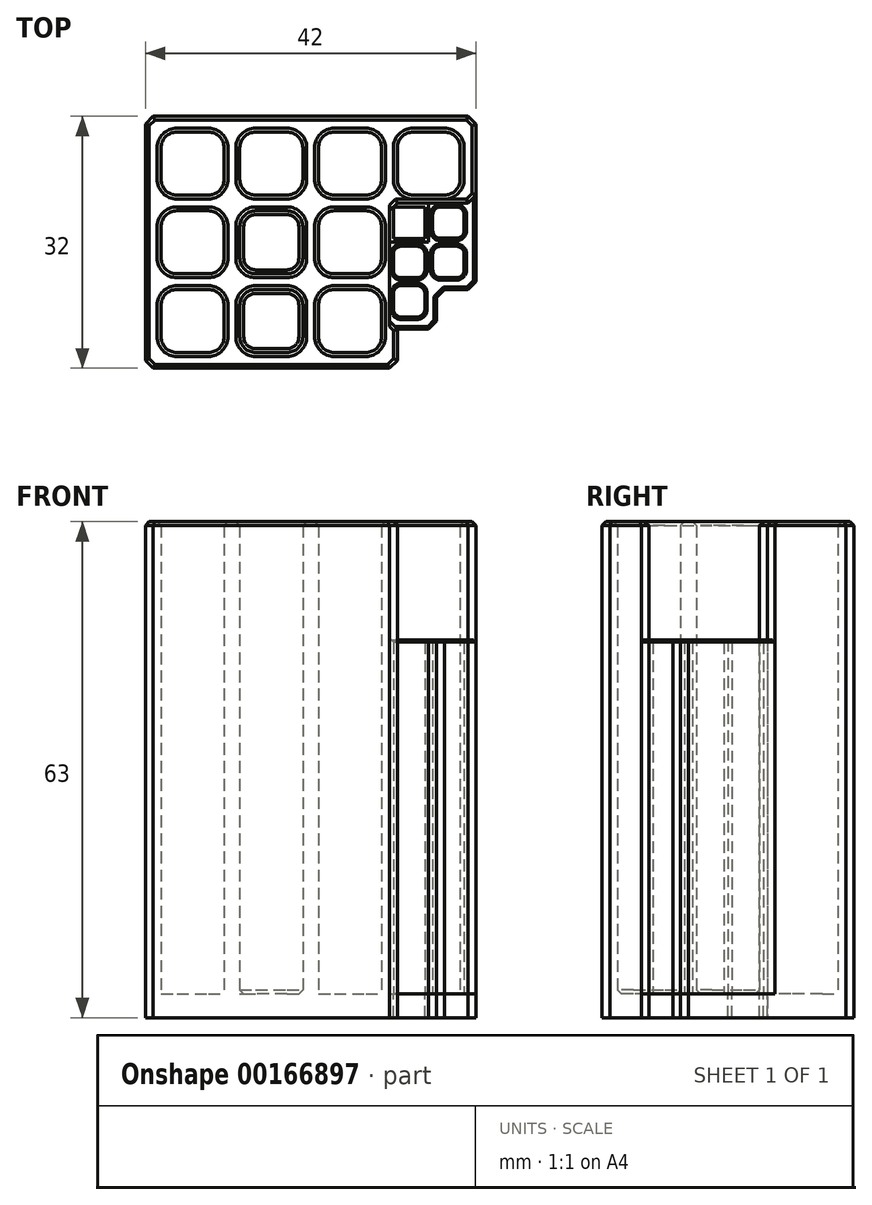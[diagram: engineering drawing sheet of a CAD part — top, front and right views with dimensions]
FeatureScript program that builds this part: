
annotation { "Feature Type Name" : "Feature", "Feature Type Description" : "" }
export const myFeature = defineFeature(function(context is Context, id is Id, definition is map)
    precondition{}
    {
        {
            var Q0;
            Q0=qCreatedBy(makeId("Top.planeOp"),FACE);
            var sketch = newSketch(context, id + "F0", { "sketchPlane" : qUnion([Q0])});
            skLineSegment(sketch, "E0.bottom", {"start": v(-42.55, 29) * mm, "end": v(-34.55, 29) * mm});
            skLineSegment(sketch, "E0.top", {"start": v(-42.55, 21) * mm, "end": v(-34.55, 21) * mm});
            skLineSegment(sketch, "E0.left", {"start": v(-42.55, 29) * mm, "end": v(-42.55, 21) * mm});
            skLineSegment(sketch, "E0.right", {"start": v(-34.55, 29) * mm, "end": v(-34.55, 21) * mm});
            skLineSegment(sketch, "E1", {"start": v(-42.55, 29) * mm, "end": v(-34.55, 21) * mm, "construction": true});
            skPoint(sketch, "E2", {"position": v(-38.55, 25) * mm});
            skLineSegment(sketch, "E3.bottom", {"start": v(-43.55, 30) * mm, "end": v(-33.55, 30) * mm});
            skLineSegment(sketch, "E3.top", {"start": v(-43.55, 20) * mm, "end": v(-33.55, 20) * mm});
            skLineSegment(sketch, "E3.left", {"start": v(-43.55, 30) * mm, "end": v(-43.55, 20) * mm});
            skLineSegment(sketch, "E3.right", {"start": v(-33.55, 30) * mm, "end": v(-33.55, 20) * mm});
            skLineSegment(sketch, "E4.bottom", {"start": v(-33.55, 30) * mm, "end": v(-23.55, 30) * mm});
            skLineSegment(sketch, "E4.top", {"start": v(-33.55, 20) * mm, "end": v(-23.55, 20) * mm});
            skLineSegment(sketch, "E4.right", {"start": v(-23.55, 30) * mm, "end": v(-23.55, 20) * mm});
            skLineSegment(sketch, "E5.bottom", {"start": v(-23.55, 30) * mm, "end": v(-13.55, 30) * mm});
            skLineSegment(sketch, "E5.top", {"start": v(-23.55, 20) * mm, "end": v(-13.55, 20) * mm});
            skLineSegment(sketch, "E5.right", {"start": v(-13.55, 30) * mm, "end": v(-13.55, 20) * mm});
            skLineSegment(sketch, "E6.top", {"start": v(-43.55, 10) * mm, "end": v(-33.55, 10) * mm});
            skLineSegment(sketch, "E6.left", {"start": v(-43.55, 20) * mm, "end": v(-43.55, 10) * mm});
            skLineSegment(sketch, "E6.right", {"start": v(-33.55, 20) * mm, "end": v(-33.55, 10) * mm});
            skLineSegment(sketch, "E7.top", {"start": v(-33.55, 10) * mm, "end": v(-23.55, 10) * mm});
            skLineSegment(sketch, "E7.right", {"start": v(-23.55, 20) * mm, "end": v(-23.55, 10) * mm});
            skLineSegment(sketch, "E8.top", {"start": v(-23.55, 10) * mm, "end": v(-13.55, 10) * mm});
            skLineSegment(sketch, "E8.right", {"start": v(-13.55, 20) * mm, "end": v(-13.55, 10) * mm});
            skLineSegment(sketch, "E9.top", {"start": v(-43.55, 0) * mm, "end": v(-33.55, 0) * mm});
            skLineSegment(sketch, "E9.left", {"start": v(-43.55, 10) * mm, "end": v(-43.55, 0) * mm});
            skLineSegment(sketch, "E9.right", {"start": v(-33.55, 10) * mm, "end": v(-33.55, 0) * mm});
            skLineSegment(sketch, "E10.top", {"start": v(-33.55, 0) * mm, "end": v(-23.55, 0) * mm});
            skLineSegment(sketch, "E10.right", {"start": v(-23.55, 10) * mm, "end": v(-23.55, 0) * mm});
            skLineSegment(sketch, "E11.top", {"start": v(-23.55, 0) * mm, "end": v(-13.55, 0) * mm});
            skLineSegment(sketch, "E11.right", {"start": v(-13.55, 10) * mm, "end": v(-13.55, 0) * mm});
            skLineSegment(sketch, "E12", {"start": v(-33.55, 30) * mm, "end": v(-23.55, 20) * mm, "construction": true});
            skLineSegment(sketch, "E13", {"start": v(-33.55, 20) * mm, "end": v(-23.55, 10) * mm, "construction": true});
            skLineSegment(sketch, "E14", {"start": v(-43.55, 20) * mm, "end": v(-33.55, 10) * mm, "construction": true});
            skLineSegment(sketch, "E15", {"start": v(-43.55, 10) * mm, "end": v(-33.55, 0) * mm, "construction": true});
            skLineSegment(sketch, "E16", {"start": v(-33.55, 10) * mm, "end": v(-23.55, 0) * mm, "construction": true});
            skLineSegment(sketch, "E17", {"start": v(-23.55, 10) * mm, "end": v(-13.55, 0) * mm, "construction": true});
            skLineSegment(sketch, "E18", {"start": v(-23.55, 20) * mm, "end": v(-13.55, 10) * mm, "construction": true});
            skPoint(sketch, "E19", {"position": v(-28.55, 25) * mm});
            skPoint(sketch, "E20", {"position": v(-18.55, 15) * mm});
            skPoint(sketch, "E21", {"position": v(-28.55, 15) * mm});
            skPoint(sketch, "E22", {"position": v(-38.55, 15) * mm});
            skPoint(sketch, "E23", {"position": v(-38.55, 5) * mm});
            skPoint(sketch, "E24", {"position": v(-28.55, 5) * mm});
            skPoint(sketch, "E25", {"position": v(-18.55, 5) * mm});
            skLineSegment(sketch, "E26.bottom", {"start": v(-24.55, 29) * mm, "end": v(-32.55, 29) * mm});
            skLineSegment(sketch, "E26.top", {"start": v(-24.55, 21) * mm, "end": v(-32.55, 21) * mm});
            skLineSegment(sketch, "E26.left", {"start": v(-24.55, 29) * mm, "end": v(-24.55, 21) * mm});
            skLineSegment(sketch, "E26.right", {"start": v(-32.55, 29) * mm, "end": v(-32.55, 21) * mm});
            skLineSegment(sketch, "E27", {"start": v(-23.55, 30) * mm, "end": v(-13.55, 20) * mm, "construction": true});
            skPoint(sketch, "E28", {"position": v(-18.55, 25) * mm});
            skLineSegment(sketch, "E29.bottom", {"start": v(-22.55, 29) * mm, "end": v(-14.55, 29) * mm});
            skLineSegment(sketch, "E29.top", {"start": v(-22.55, 21) * mm, "end": v(-14.55, 21) * mm});
            skLineSegment(sketch, "E29.left", {"start": v(-22.55, 29) * mm, "end": v(-22.55, 21) * mm});
            skLineSegment(sketch, "E29.right", {"start": v(-14.55, 29) * mm, "end": v(-14.55, 21) * mm});
            skLineSegment(sketch, "E30.bottom", {"start": v(-22.55, 19) * mm, "end": v(-14.55, 19) * mm});
            skLineSegment(sketch, "E30.top", {"start": v(-22.55, 11) * mm, "end": v(-14.55, 11) * mm});
            skLineSegment(sketch, "E30.left", {"start": v(-22.55, 19) * mm, "end": v(-22.55, 11) * mm});
            skLineSegment(sketch, "E30.right", {"start": v(-14.55, 19) * mm, "end": v(-14.55, 11) * mm});
            skLineSegment(sketch, "E31.bottom", {"start": v(-22.55, 9) * mm, "end": v(-14.55, 9) * mm});
            skLineSegment(sketch, "E31.top", {"start": v(-22.55, 1) * mm, "end": v(-14.55, 1) * mm});
            skLineSegment(sketch, "E31.left", {"start": v(-22.55, 9) * mm, "end": v(-22.55, 1) * mm});
            skLineSegment(sketch, "E31.right", {"start": v(-14.55, 9) * mm, "end": v(-14.55, 1) * mm});
            skLineSegment(sketch, "E32.bottom", {"start": v(-32.55, 9) * mm, "end": v(-24.55, 9) * mm});
            skLineSegment(sketch, "E32.top", {"start": v(-32.55, 1) * mm, "end": v(-24.55, 1) * mm});
            skLineSegment(sketch, "E32.left", {"start": v(-32.55, 9) * mm, "end": v(-32.55, 1) * mm});
            skLineSegment(sketch, "E32.right", {"start": v(-24.55, 9) * mm, "end": v(-24.55, 1) * mm});
            skLineSegment(sketch, "E33.bottom", {"start": v(-42.55, 9) * mm, "end": v(-34.55, 9) * mm});
            skLineSegment(sketch, "E33.top", {"start": v(-42.55, 1) * mm, "end": v(-34.55, 1) * mm});
            skLineSegment(sketch, "E33.left", {"start": v(-42.55, 9) * mm, "end": v(-42.55, 1) * mm});
            skLineSegment(sketch, "E33.right", {"start": v(-34.55, 9) * mm, "end": v(-34.55, 1) * mm});
            skLineSegment(sketch, "E34.bottom", {"start": v(-42.55, 19) * mm, "end": v(-34.55, 19) * mm});
            skLineSegment(sketch, "E34.top", {"start": v(-42.55, 11) * mm, "end": v(-34.55, 11) * mm});
            skLineSegment(sketch, "E34.left", {"start": v(-42.55, 19) * mm, "end": v(-42.55, 11) * mm});
            skLineSegment(sketch, "E34.right", {"start": v(-34.55, 19) * mm, "end": v(-34.55, 11) * mm});
            skLineSegment(sketch, "E35.bottom", {"start": v(-32.55, 19) * mm, "end": v(-24.55, 19) * mm});
            skLineSegment(sketch, "E35.top", {"start": v(-32.55, 11) * mm, "end": v(-24.55, 11) * mm});
            skLineSegment(sketch, "E35.left", {"start": v(-32.55, 19) * mm, "end": v(-32.55, 11) * mm});
            skLineSegment(sketch, "E35.right", {"start": v(-24.55, 19) * mm, "end": v(-24.55, 11) * mm});
            skLineSegment(sketch, "E36.left", {"start": v(-13.55, 0) * mm, "end": v(-13.55, 6) * mm});
            skLineSegment(sketch, "E37.left", {"start": v(-13.55, 6) * mm, "end": v(-13.55, 12) * mm});
            skLineSegment(sketch, "E38.left", {"start": v(-13.55, 12) * mm, "end": v(-13.55, 18) * mm});
            skLineSegment(sketch, "E39.bottom", {"start": v(-13.55, 30) * mm, "end": v(-3.55, 30) * mm});
            skLineSegment(sketch, "E39.top", {"start": v(-13.55, 20) * mm, "end": v(-3.55, 20) * mm});
            skLineSegment(sketch, "E39.right", {"start": v(-3.55, 30) * mm, "end": v(-3.55, 20) * mm});
            skLineSegment(sketch, "E40", {"start": v(-13.55, 30) * mm, "end": v(-3.55, 20) * mm, "construction": true});
            skPoint(sketch, "E41", {"position": v(-8.55, 25) * mm});
            skLineSegment(sketch, "E42.bottom", {"start": v(-4.55, 29) * mm, "end": v(-12.55, 29) * mm});
            skLineSegment(sketch, "E42.top", {"start": v(-4.55, 21) * mm, "end": v(-12.55, 21) * mm});
            skLineSegment(sketch, "E42.left", {"start": v(-4.55, 29) * mm, "end": v(-4.55, 21) * mm});
            skLineSegment(sketch, "E42.right", {"start": v(-12.55, 29) * mm, "end": v(-12.55, 21) * mm});
            skLineSegment(sketch, "E43.bottom", {"start": v(-13.55, 20) * mm, "end": v(-8.55, 20) * mm});
            skLineSegment(sketch, "E43.top", {"start": v(-13.55, 15) * mm, "end": v(-8.55, 15) * mm});
            skLineSegment(sketch, "E43.left", {"start": v(-13.55, 20) * mm, "end": v(-13.55, 15) * mm});
            skLineSegment(sketch, "E43.right", {"start": v(-8.55, 20) * mm, "end": v(-8.55, 15) * mm});
            skLineSegment(sketch, "E44.top", {"start": v(-13.55, 10) * mm, "end": v(-8.55, 10) * mm});
            skLineSegment(sketch, "E44.left", {"start": v(-13.55, 15) * mm, "end": v(-13.55, 10) * mm});
            skLineSegment(sketch, "E44.right", {"start": v(-8.55, 15) * mm, "end": v(-8.55, 10) * mm});
            skLineSegment(sketch, "E45.top", {"start": v(-13.55, 5) * mm, "end": v(-8.55, 5) * mm});
            skLineSegment(sketch, "E45.left", {"start": v(-13.55, 10) * mm, "end": v(-13.55, 5) * mm});
            skLineSegment(sketch, "E45.right", {"start": v(-8.55, 10) * mm, "end": v(-8.55, 5) * mm});
            skLineSegment(sketch, "E46.bottom", {"start": v(-8.55, 5) * mm, "end": v(-13.55, 5) * mm});
            skLineSegment(sketch, "E46.right", {"start": v(-13.55, 5) * mm, "end": v(-13.55, 0) * mm});
            skLineSegment(sketch, "E47.bottom", {"start": v(-8.55, 20) * mm, "end": v(-3.54, 20) * mm});
            skLineSegment(sketch, "E47.top", {"start": v(-8.55, 15) * mm, "end": v(-3.54, 15) * mm});
            skLineSegment(sketch, "E47.right", {"start": v(-3.54, 20) * mm, "end": v(-3.54, 15) * mm});
            skLineSegment(sketch, "E48.top", {"start": v(-8.55, 10) * mm, "end": v(-3.54, 10) * mm});
            skLineSegment(sketch, "E48.right", {"start": v(-3.54, 15) * mm, "end": v(-3.54, 10) * mm});
            skLineSegment(sketch, "E49", {"start": v(-13.55, 20) * mm, "end": v(-8.55, 15) * mm, "construction": true});
            skLineSegment(sketch, "E50", {"start": v(-13.55, 10) * mm, "end": v(-8.55, 5) * mm, "construction": true});
            skLineSegment(sketch, "E51", {"start": v(-8.55, 15) * mm, "end": v(-3.54, 10) * mm, "construction": true});
            skLineSegment(sketch, "E52", {"start": v(-13.55, 15) * mm, "end": v(-8.55, 10) * mm, "construction": true});
            skLineSegment(sketch, "E53", {"start": v(-8.55, 20) * mm, "end": v(-3.54, 15) * mm, "construction": true});
            skPoint(sketch, "E54", {"position": v(-11.05, 17.5) * mm});
            skPoint(sketch, "E55", {"position": v(-6.04, 17.5) * mm});
            skPoint(sketch, "E56", {"position": v(-11.05, 12.5) * mm});
            skPoint(sketch, "E57", {"position": v(-6.04, 12.5) * mm});
            skPoint(sketch, "E58", {"position": v(-11.05, 7.5) * mm});
            skLineSegment(sketch, "E59.bottom", {"start": v(-9.05, 19.5) * mm, "end": v(-13.05, 19.5) * mm});
            skLineSegment(sketch, "E59.top", {"start": v(-9.05, 15.5) * mm, "end": v(-13.05, 15.5) * mm});
            skLineSegment(sketch, "E59.left", {"start": v(-9.05, 19.5) * mm, "end": v(-9.05, 15.5) * mm});
            skLineSegment(sketch, "E59.right", {"start": v(-13.05, 19.5) * mm, "end": v(-13.05, 15.5) * mm});
            skLineSegment(sketch, "E60.bottom", {"start": v(-13.05, 14.5) * mm, "end": v(-9.05, 14.5) * mm});
            skLineSegment(sketch, "E60.top", {"start": v(-13.05, 10.5) * mm, "end": v(-9.05, 10.5) * mm});
            skLineSegment(sketch, "E60.left", {"start": v(-13.05, 14.5) * mm, "end": v(-13.05, 10.5) * mm});
            skLineSegment(sketch, "E60.right", {"start": v(-9.05, 14.5) * mm, "end": v(-9.05, 10.5) * mm});
            skLineSegment(sketch, "E61.bottom", {"start": v(-13.05, 9.5) * mm, "end": v(-9.05, 9.5) * mm});
            skLineSegment(sketch, "E61.top", {"start": v(-13.05, 5.5) * mm, "end": v(-9.05, 5.5) * mm});
            skLineSegment(sketch, "E61.left", {"start": v(-13.05, 9.5) * mm, "end": v(-13.05, 5.5) * mm});
            skLineSegment(sketch, "E61.right", {"start": v(-9.05, 9.5) * mm, "end": v(-9.05, 5.5) * mm});
            skLineSegment(sketch, "E62.bottom", {"start": v(-4.04, 15.5) * mm, "end": v(-8.04, 15.5) * mm});
            skLineSegment(sketch, "E62.top", {"start": v(-4.04, 19.5) * mm, "end": v(-8.04, 19.5) * mm});
            skLineSegment(sketch, "E62.left", {"start": v(-4.04, 15.5) * mm, "end": v(-4.04, 19.5) * mm});
            skLineSegment(sketch, "E62.right", {"start": v(-8.04, 15.5) * mm, "end": v(-8.04, 19.5) * mm});
            skLineSegment(sketch, "E63.bottom", {"start": v(-4.04, 10.5) * mm, "end": v(-8.04, 10.5) * mm});
            skLineSegment(sketch, "E63.top", {"start": v(-4.04, 14.5) * mm, "end": v(-8.04, 14.5) * mm});
            skLineSegment(sketch, "E63.left", {"start": v(-4.04, 10.5) * mm, "end": v(-4.04, 14.5) * mm});
            skLineSegment(sketch, "E63.right", {"start": v(-8.04, 10.5) * mm, "end": v(-8.04, 14.5) * mm});
            skLineSegment(sketch, "E64", {"start": v(-44.55, 30) * mm, "end": v(-44.55, 0) * mm});
            skLineSegment(sketch, "E65", {"start": v(-44.55, 0) * mm, "end": v(-44.55, -1) * mm});
            skLineSegment(sketch, "E66", {"start": v(-44.55, -1) * mm, "end": v(-13.55, -1) * mm});
            skLineSegment(sketch, "E67", {"start": v(-13.55, -1) * mm, "end": v(-12.55, -1) * mm});
            skLineSegment(sketch, "E68", {"start": v(-12.55, -1) * mm, "end": v(-12.55, 5) * mm});
            skLineSegment(sketch, "E69", {"start": v(-44.55, 30) * mm, "end": v(-44.55, 31) * mm});
            skLineSegment(sketch, "E70", {"start": v(-44.55, 31) * mm, "end": v(-3.55, 31) * mm});
            skLineSegment(sketch, "E71", {"start": v(-3.55, 31) * mm, "end": v(-2.55, 31) * mm});
            skLineSegment(sketch, "E72", {"start": v(-2.55, 31) * mm, "end": v(-2.55, 10) * mm});
            skLineSegment(sketch, "E73", {"start": v(-2.55, 10) * mm, "end": v(-2.55, 9) * mm});
            skLineSegment(sketch, "E74", {"start": v(-2.55, 9) * mm, "end": v(-8.55, 9) * mm});
            skLineSegment(sketch, "E75", {"start": v(-8.55, 5) * mm, "end": v(-8.55, 4) * mm});
            skLineSegment(sketch, "E76", {"start": v(-8.55, 4) * mm, "end": v(-12.55, 4) * mm});
            skLineSegment(sketch, "E77", {"start": v(-8.55, 4) * mm, "end": v(-7.55, 4) * mm});
            skLineSegment(sketch, "E78", {"start": v(-7.55, 4) * mm, "end": v(-7.55, 9) * mm});
            skLineSegment(sketch, "E79", {"start": v(-13.55, 5) * mm, "end": v(-12.55, 4) * mm});
            skLineSegment(sketch, "E80", {"start": v(-3.54, 20) * mm, "end": v(-2.55, 20) * mm});
            skLineSegment(sketch, "E81", {"start": v(-3.54, 20) * mm, "end": v(-2.54, 21) * mm});
            skSolve(sketch);
        }
        {
            var Q0;
            Q0=makeQuery(id+"F0.imprint","IMPRINT",FACE,{"disambiguationData":[TD([[makeQuery(id+"F0.imprint","IMPRINT",EDGE,{"derivedFrom":sQuery(id+"F0.wireOp",EDGE,"E3.bottom")}),1.0]])]});
            var Q1;
            Q1=makeQuery(id+"F0.imprint","IMPRINT",FACE,{"disambiguationData":[TD([[makeQuery(id+"F0.imprint","IMPRINT",EDGE,{"derivedFrom":sQuery(id+"F0.wireOp",EDGE,"E0.bottom")}),1.0]])]});
            var Q2;
            Q2=makeQuery(id+"F0.imprint","IMPRINT",FACE,{"disambiguationData":[TD([[makeQuery(id+"F0.imprint","IMPRINT",EDGE,{"derivedFrom":sQuery(id+"F0.wireOp",EDGE,"E4.bottom")}),-1.0]])]});
            var Q3;
            Q3=makeQuery(id+"F0.imprint","IMPRINT",FACE,{"disambiguationData":[TD([[makeQuery(id+"F0.imprint","IMPRINT",EDGE,{"derivedFrom":sQuery(id+"F0.wireOp",EDGE,"E3.top")}),-1.0]])]});
            var Q4;
            Q4=makeQuery(id+"F0.imprint","IMPRINT",FACE,{"disambiguationData":[TD([[makeQuery(id+"F0.imprint","IMPRINT",EDGE,{"derivedFrom":sQuery(id+"F0.wireOp",EDGE,"E4.top")}),-1.0]])]});
            var Q5;
            Q5=makeQuery(id+"F0.imprint","IMPRINT",FACE,{"disambiguationData":[TD([[makeQuery(id+"F0.imprint","IMPRINT",EDGE,{"derivedFrom":sQuery(id+"F0.wireOp",EDGE,"E6.top")}),-1.0]])]});
            var Q6;
            Q6=makeQuery(id+"F0.imprint","IMPRINT",FACE,{"disambiguationData":[TD([[makeQuery(id+"F0.imprint","IMPRINT",EDGE,{"derivedFrom":sQuery(id+"F0.wireOp",EDGE,"E7.top")}),-1.0]])]});
            var Q7;
            {var subQ0=sQuery(id+"F0.wireOp",EDGE,"E8.top");Q7=makeQuery(id+"F0.imprint","IMPRINT",FACE,{"disambiguationData":[TD([[makeQuery(id+"F0.imprint","IMPRINT",EDGE,{"derivedFrom":subQ0}),-1.0]])]});}
            var Q8;
            {var subQ6=sQuery(id+"F0.wireOp",EDGE,"E5.top");Q8=makeQuery(id+"F0.imprint","IMPRINT",FACE,{"disambiguationData":[TD([[makeQuery(id+"F0.imprint","IMPRINT",EDGE,{"derivedFrom":subQ6}),-1.0]])]});}
            var Q9;
            Q9=makeQuery(id+"F0.imprint","IMPRINT",FACE,{"disambiguationData":[TD([[makeQuery(id+"F0.imprint","IMPRINT",EDGE,{"derivedFrom":sQuery(id+"F0.wireOp",EDGE,"E47.top")}),-1.0]])]});
            var Q10;
            Q10=makeQuery(id+"F0.imprint","IMPRINT",FACE,{"disambiguationData":[TD([[makeQuery(id+"F0.imprint","IMPRINT",EDGE,{"derivedFrom":sQuery(id+"F0.wireOp",EDGE,"E61.bottom")}),-1.0]])]});
            var Q11;
            Q11=makeQuery(id+"F0.imprint","IMPRINT",FACE,{"disambiguationData":[TD([[makeQuery(id+"F0.imprint","IMPRINT",EDGE,{"derivedFrom":sQuery(id+"F0.wireOp",EDGE,"E60.bottom")}),-1.0]])]});
            var Q12;
            Q12=makeQuery(id+"F0.imprint","IMPRINT",FACE,{"disambiguationData":[TD([[makeQuery(id+"F0.imprint","IMPRINT",EDGE,{"derivedFrom":sQuery(id+"F0.wireOp",EDGE,"E59.bottom")}),1.0]])]});
            var Q13;
            Q13=makeQuery(id+"F0.imprint","IMPRINT",FACE,{"disambiguationData":[TD([[makeQuery(id+"F0.imprint","IMPRINT",EDGE,{"derivedFrom":sQuery(id+"F0.wireOp",EDGE,"E42.bottom")}),1.0]])]});
            var Q14;
            Q14=makeQuery(id+"F0.imprint","IMPRINT",FACE,{"disambiguationData":[TD([[makeQuery(id+"F0.imprint","IMPRINT",EDGE,{"derivedFrom":sQuery(id+"F0.wireOp",EDGE,"E35.bottom")}),-1.0]])]});
            var Q15;
            Q15=makeQuery(id+"F0.imprint","IMPRINT",FACE,{"disambiguationData":[TD([[makeQuery(id+"F0.imprint","IMPRINT",EDGE,{"derivedFrom":sQuery(id+"F0.wireOp",EDGE,"E34.bottom")}),-1.0]])]});
            var Q16;
            Q16=makeQuery(id+"F0.imprint","IMPRINT",FACE,{"disambiguationData":[TD([[makeQuery(id+"F0.imprint","IMPRINT",EDGE,{"derivedFrom":sQuery(id+"F0.wireOp",EDGE,"E33.bottom")}),-1.0]])]});
            var Q17;
            Q17=makeQuery(id+"F0.imprint","IMPRINT",FACE,{"disambiguationData":[TD([[makeQuery(id+"F0.imprint","IMPRINT",EDGE,{"derivedFrom":sQuery(id+"F0.wireOp",EDGE,"E32.bottom")}),-1.0]])]});
            var Q18;
            Q18=makeQuery(id+"F0.imprint","IMPRINT",FACE,{"disambiguationData":[TD([[makeQuery(id+"F0.imprint","IMPRINT",EDGE,{"derivedFrom":sQuery(id+"F0.wireOp",EDGE,"E31.bottom")}),-1.0]])]});
            var Q19;
            Q19=makeQuery(id+"F0.imprint","IMPRINT",FACE,{"disambiguationData":[TD([[makeQuery(id+"F0.imprint","IMPRINT",EDGE,{"derivedFrom":sQuery(id+"F0.wireOp",EDGE,"E30.bottom")}),-1.0]])]});
            var Q20;
            Q20=makeQuery(id+"F0.imprint","IMPRINT",FACE,{"disambiguationData":[TD([[makeQuery(id+"F0.imprint","IMPRINT",EDGE,{"derivedFrom":sQuery(id+"F0.wireOp",EDGE,"E29.bottom")}),-1.0]])]});
            var Q21;
            Q21=makeQuery(id+"F0.imprint","IMPRINT",FACE,{"disambiguationData":[TD([[makeQuery(id+"F0.imprint","IMPRINT",EDGE,{"derivedFrom":sQuery(id+"F0.wireOp",EDGE,"E26.bottom")}),1.0]])]});
            var Q22;
            Q22=makeQuery(id+"F0.imprint","IMPRINT",FACE,{"disambiguationData":[TD([[makeQuery(id+"F0.imprint","IMPRINT",EDGE,{"derivedFrom":sQuery(id+"F0.wireOp",EDGE,"E0.bottom")}),-1.0]])]});
            var Q23;
            {var subQ7=sQuery(id+"F0.wireOp",EDGE,"E44.top");Q23=makeQuery(id+"F0.imprint","IMPRINT",FACE,{"disambiguationData":[TD([[makeQuery(id+"F0.imprint","IMPRINT",EDGE,{"derivedFrom":subQ7}),-1.0]])]});}
            var Q24;
            {var subQ0=sQuery(id+"F0.wireOp",EDGE,"E79");Q24=makeQuery(id+"F0.imprint","IMPRINT",FACE,{"disambiguationData":[TD([[makeQuery(id+"F0.imprint","IMPRINT",EDGE,{"derivedFrom":subQ0}),1.0]])]});}
            var Q25;
            Q25=makeQuery(id+"F0.imprint","IMPRINT",FACE,{"disambiguationData":[TD([[makeQuery(id+"F0.imprint","IMPRINT",EDGE,{"derivedFrom":sQuery(id+"F0.wireOp",EDGE,"E63.bottom")}),-1.0]])]});
            var Q26;
            Q26=makeQuery(id+"F0.imprint","IMPRINT",FACE,{"disambiguationData":[TD([[makeQuery(id+"F0.imprint","IMPRINT",EDGE,{"derivedFrom":sQuery(id+"F0.wireOp",EDGE,"E62.bottom")}),-1.0]])]});
            var Q27;
            {var subQ1=sQuery(id+"F0.wireOp",EDGE,"E43.right");Q27=makeQuery(id+"F0.imprint","IMPRINT",FACE,{"disambiguationData":[TD([[makeQuery(id+"F0.imprint","IMPRINT",EDGE,{"derivedFrom":subQ1}),1.0]])]});}
            var Q28;
            {var subQ0=sQuery(id+"F0.wireOp",EDGE,"E75");Q28=makeQuery(id+"F0.imprint","IMPRINT",FACE,{"disambiguationData":[TD([[makeQuery(id+"F0.imprint","IMPRINT",EDGE,{"derivedFrom":subQ0}),-1.0]])]});}
            var Q29;
            {var subQ4=sQuery(id+"F0.wireOp",EDGE,"E75");Q29=makeQuery(id+"F0.imprint","IMPRINT",FACE,{"disambiguationData":[TD([[makeQuery(id+"F0.imprint","IMPRINT",EDGE,{"derivedFrom":subQ4}),1.0]])]});}
            var Q30;
            Q30=makeQuery(id+"F0.imprint","IMPRINT",FACE,{"disambiguationData":[TD([[makeQuery(id+"F0.imprint","IMPRINT",EDGE,{"derivedFrom":sQuery(id+"F0.wireOp",EDGE,"E5.bottom")}),-1.0]])]});
            var Q31;
            {var subQ3=sQuery(id+"F0.wireOp",EDGE,"E43.bottom");Q31=makeQuery(id+"F0.imprint","IMPRINT",FACE,{"disambiguationData":[TD([[makeQuery(id+"F0.imprint","IMPRINT",EDGE,{"derivedFrom":subQ3}),-1.0]])]});}
            var Q32;
            Q32=makeQuery(id+"F0.imprint","IMPRINT",FACE,{"disambiguationData":[TD([[makeQuery(id+"F0.imprint","IMPRINT",EDGE,{"derivedFrom":sQuery(id+"F0.wireOp",EDGE,"E47.right")}),1.0]])]});
            var Q33;
            Q33=makeQuery(id+"F0.imprint","IMPRINT",FACE,{"disambiguationData":[TD([[makeQuery(id+"F0.imprint","IMPRINT",EDGE,{"derivedFrom":sQuery(id+"F0.wireOp",EDGE,"E39.bottom")}),-1.0]])]});
            var Q34;
            {var subQ3=sQuery(id+"F0.wireOp",EDGE,"E43.top");Q34=makeQuery(id+"F0.imprint","IMPRINT",FACE,{"disambiguationData":[TD([[makeQuery(id+"F0.imprint","IMPRINT",EDGE,{"derivedFrom":subQ3}),-1.0]])]});}
            var Q35;
            {var subQ0=sQuery(id+"F0.wireOp",EDGE,"E80");Q35=makeQuery(id+"F0.imprint","IMPRINT",FACE,{"disambiguationData":[TD([[makeQuery(id+"F0.imprint","IMPRINT",EDGE,{"derivedFrom":subQ0}),1.0]])]});}
            extrude(context, id + "F1", {"entities" : qUnion([Q0, Q1, Q2, Q3, Q4, Q5, Q6, Q7, Q8, Q9, Q10, Q11, Q12, Q13, Q14, Q15, Q16, Q17, Q18, Q19, Q20, Q21, Q22, Q23, Q24, Q25, Q26, Q27, Q28, Q29, Q30, Q31, Q32, Q33, Q34, Q35]), "oppositeDirection" : true, "depth" : 3 * mm});
        }
        {
            var Q0;
            Q0=makeQuery(id+"F0.imprint","IMPRINT",FACE,{"disambiguationData":[TD([[makeQuery(id+"F0.imprint","IMPRINT",EDGE,{"derivedFrom":sQuery(id+"F0.wireOp",EDGE,"E3.bottom")}),1.0]])]});
            var Q1;
            Q1=makeQuery(id+"F0.imprint","IMPRINT",FACE,{"disambiguationData":[TD([[makeQuery(id+"F0.imprint","IMPRINT",EDGE,{"derivedFrom":sQuery(id+"F0.wireOp",EDGE,"E0.bottom")}),1.0]])]});
            var Q2;
            Q2=makeQuery(id+"F0.imprint","IMPRINT",FACE,{"disambiguationData":[TD([[makeQuery(id+"F0.imprint","IMPRINT",EDGE,{"derivedFrom":sQuery(id+"F0.wireOp",EDGE,"E4.bottom")}),-1.0]])]});
            var Q3;
            Q3=makeQuery(id+"F0.imprint","IMPRINT",FACE,{"disambiguationData":[TD([[makeQuery(id+"F0.imprint","IMPRINT",EDGE,{"derivedFrom":sQuery(id+"F0.wireOp",EDGE,"E3.top")}),-1.0]])]});
            var Q4;
            Q4=makeQuery(id+"F0.imprint","IMPRINT",FACE,{"disambiguationData":[TD([[makeQuery(id+"F0.imprint","IMPRINT",EDGE,{"derivedFrom":sQuery(id+"F0.wireOp",EDGE,"E4.top")}),-1.0]])]});
            var Q5;
            Q5=makeQuery(id+"F0.imprint","IMPRINT",FACE,{"disambiguationData":[TD([[makeQuery(id+"F0.imprint","IMPRINT",EDGE,{"derivedFrom":sQuery(id+"F0.wireOp",EDGE,"E6.top")}),-1.0]])]});
            var Q6;
            Q6=makeQuery(id+"F0.imprint","IMPRINT",FACE,{"disambiguationData":[TD([[makeQuery(id+"F0.imprint","IMPRINT",EDGE,{"derivedFrom":sQuery(id+"F0.wireOp",EDGE,"E7.top")}),-1.0]])]});
            var Q7;
            {var subQ0=sQuery(id+"F0.wireOp",EDGE,"E8.top");Q7=makeQuery(id+"F0.imprint","IMPRINT",FACE,{"disambiguationData":[TD([[makeQuery(id+"F0.imprint","IMPRINT",EDGE,{"derivedFrom":subQ0}),-1.0]])]});}
            var Q8;
            {var subQ6=sQuery(id+"F0.wireOp",EDGE,"E5.top");Q8=makeQuery(id+"F0.imprint","IMPRINT",FACE,{"disambiguationData":[TD([[makeQuery(id+"F0.imprint","IMPRINT",EDGE,{"derivedFrom":subQ6}),-1.0]])]});}
            var Q9;
            Q9=makeQuery(id+"F0.imprint","IMPRINT",FACE,{"disambiguationData":[TD([[makeQuery(id+"F0.imprint","IMPRINT",EDGE,{"derivedFrom":sQuery(id+"F0.wireOp",EDGE,"E5.bottom")}),-1.0]])]});
            var Q10;
            Q10=makeQuery(id+"F0.imprint","IMPRINT",FACE,{"disambiguationData":[TD([[makeQuery(id+"F0.imprint","IMPRINT",EDGE,{"derivedFrom":sQuery(id+"F0.wireOp",EDGE,"E39.bottom")}),-1.0]])]});
            extrude(context, id + "F2", {"entities" : qUnion([Q0, Q1, Q2, Q3, Q4, Q5, Q6, Q7, Q8, Q9, Q10]), "operationType" : NewBodyOperationType.ADD, "depth" : 60 * mm});
        }
        {
            var Q0;
            {var subQ3=sQuery(id+"F0.wireOp",EDGE,"E43.bottom");Q0=makeQuery(id+"F0.imprint","IMPRINT",FACE,{"disambiguationData":[TD([[makeQuery(id+"F0.imprint","IMPRINT",EDGE,{"derivedFrom":subQ3}),-1.0]])]});}
            var Q1;
            {var subQ3=sQuery(id+"F0.wireOp",EDGE,"E43.top");Q1=makeQuery(id+"F0.imprint","IMPRINT",FACE,{"disambiguationData":[TD([[makeQuery(id+"F0.imprint","IMPRINT",EDGE,{"derivedFrom":subQ3}),-1.0]])]});}
            var Q2;
            {var subQ7=sQuery(id+"F0.wireOp",EDGE,"E44.top");Q2=makeQuery(id+"F0.imprint","IMPRINT",FACE,{"disambiguationData":[TD([[makeQuery(id+"F0.imprint","IMPRINT",EDGE,{"derivedFrom":subQ7}),-1.0]])]});}
            var Q3;
            Q3=makeQuery(id+"F0.imprint","IMPRINT",FACE,{"disambiguationData":[TD([[makeQuery(id+"F0.imprint","IMPRINT",EDGE,{"derivedFrom":sQuery(id+"F0.wireOp",EDGE,"E47.top")}),-1.0]])]});
            var Q4;
            {var subQ1=sQuery(id+"F0.wireOp",EDGE,"E43.right");Q4=makeQuery(id+"F0.imprint","IMPRINT",FACE,{"disambiguationData":[TD([[makeQuery(id+"F0.imprint","IMPRINT",EDGE,{"derivedFrom":subQ1}),1.0]])]});}
            var Q5;
            Q5=makeQuery(id+"F0.imprint","IMPRINT",FACE,{"disambiguationData":[TD([[makeQuery(id+"F0.imprint","IMPRINT",EDGE,{"derivedFrom":sQuery(id+"F0.wireOp",EDGE,"E47.right")}),1.0]])]});
            var Q6;
            {var subQ4=sQuery(id+"F0.wireOp",EDGE,"E75");Q6=makeQuery(id+"F0.imprint","IMPRINT",FACE,{"disambiguationData":[TD([[makeQuery(id+"F0.imprint","IMPRINT",EDGE,{"derivedFrom":subQ4}),1.0]])]});}
            var Q7;
            {var subQ0=sQuery(id+"F0.wireOp",EDGE,"E75");Q7=makeQuery(id+"F0.imprint","IMPRINT",FACE,{"disambiguationData":[TD([[makeQuery(id+"F0.imprint","IMPRINT",EDGE,{"derivedFrom":subQ0}),-1.0]])]});}
            var Q8;
            {var subQ0=sQuery(id+"F0.wireOp",EDGE,"E79");Q8=makeQuery(id+"F0.imprint","IMPRINT",FACE,{"disambiguationData":[TD([[makeQuery(id+"F0.imprint","IMPRINT",EDGE,{"derivedFrom":subQ0}),1.0]])]});}
            var Q9;
            {var subQ0=sQuery(id+"F0.wireOp",EDGE,"E80");Q9=makeQuery(id+"F0.imprint","IMPRINT",FACE,{"disambiguationData":[TD([[makeQuery(id+"F0.imprint","IMPRINT",EDGE,{"derivedFrom":subQ0}),1.0]])]});}
            extrude(context, id + "F3", {"entities" : qUnion([Q0, Q1, Q2, Q3, Q4, Q5, Q6, Q7, Q8, Q9]), "depth" : 45 * mm});
        }
        {
            var Q0;
            {var subQ0=sQuery(id+"F0.wireOp",EDGE,"E72");var subQ1=sQuery(id+"F0.wireOp",EDGE,"E71");Q0=makeQuery(id+"F2.boolean.opBoolean","MERGE",EDGE,{"derivedFrom":[makeQuery(id+"F1.opExtrude","SWEPT_EDGE",EDGE,{"disambiguationData":[OSD([subQ1,subQ0])]}),makeQuery(id+"F2.opExtrude","SWEPT_EDGE",EDGE,{"disambiguationData":[OSD([subQ1,subQ0])]})]});}
            var Q1;
            {var subQ0=sQuery(id+"F0.wireOp",EDGE,"E70");var subQ1=sQuery(id+"F0.wireOp",EDGE,"E69");Q1=makeQuery(id+"F2.boolean.opBoolean","MERGE",EDGE,{"derivedFrom":[makeQuery(id+"F1.opExtrude","SWEPT_EDGE",EDGE,{"disambiguationData":[OSD([subQ1,subQ0])]}),makeQuery(id+"F2.opExtrude","SWEPT_EDGE",EDGE,{"disambiguationData":[OSD([subQ1,subQ0])]})]});}
            var Q2;
            {var subQ0=sQuery(id+"F0.wireOp",EDGE,"E66");var subQ1=sQuery(id+"F0.wireOp",EDGE,"E65");Q2=makeQuery(id+"F2.boolean.opBoolean","MERGE",EDGE,{"derivedFrom":[makeQuery(id+"F1.opExtrude","SWEPT_EDGE",EDGE,{"disambiguationData":[OSD([subQ1,subQ0])]}),makeQuery(id+"F2.opExtrude","SWEPT_EDGE",EDGE,{"disambiguationData":[OSD([subQ1,subQ0])]})]});}
            var Q3;
            {var subQ0=sQuery(id+"F0.wireOp",EDGE,"E68");var subQ1=sQuery(id+"F0.wireOp",EDGE,"E67");Q3=makeQuery(id+"F2.boolean.opBoolean","MERGE",EDGE,{"derivedFrom":[makeQuery(id+"F1.opExtrude","SWEPT_EDGE",EDGE,{"disambiguationData":[OSD([subQ1,subQ0])]}),makeQuery(id+"F2.opExtrude","SWEPT_EDGE",EDGE,{"disambiguationData":[OSD([subQ1,subQ0])]})]});}
            var Q4;
            Q4=makeQuery(id+"F3.opExtrude","SWEPT_EDGE",EDGE,{"disambiguationData":[OSD([sQuery(id+"F0.wireOp",EDGE,"E77"),sQuery(id+"F0.wireOp",EDGE,"E78")])]});
            var Q5;
            Q5=makeQuery(id+"F3.opExtrude","SWEPT_EDGE",EDGE,{"disambiguationData":[OSD([sQuery(id+"F0.wireOp",EDGE,"E73"),sQuery(id+"F0.wireOp",EDGE,"E74")])]});
            var Q6;
            Q6=makeQuery(id+"F3.opExtrude","SWEPT_EDGE",EDGE,{"disambiguationData":[OSD([sQuery(id+"F0.wireOp",EDGE,"E74"),sQuery(id+"F0.wireOp",EDGE,"E78")])]});
            var Q7;
            Q7=makeQuery(id+"F1.opExtrude","SWEPT_EDGE",EDGE,{"disambiguationData":[OSD([sQuery(id+"F0.wireOp",EDGE,"E77"),sQuery(id+"F0.wireOp",EDGE,"E78")])]});
            var Q8;
            Q8=makeQuery(id+"F1.opExtrude","SWEPT_EDGE",EDGE,{"disambiguationData":[OSD([sQuery(id+"F0.wireOp",EDGE,"E73"),sQuery(id+"F0.wireOp",EDGE,"E74")])]});
            var Q9;
            Q9=makeQuery(id+"F1.opExtrude","SWEPT_EDGE",EDGE,{"disambiguationData":[OSD([sQuery(id+"F0.wireOp",EDGE,"E74"),sQuery(id+"F0.wireOp",EDGE,"E78")])]});
            chamfer(context, id + "F4", {"entities" : qUnion([Q0, Q1, Q2, Q3, Q4, Q5, Q6, Q7, Q8, Q9]), "width" : 1 * mm, "tangentPropagation" : true});
        }
        {
            var Q0;
            Q0=makeQuery(id+"F2.opExtrude","SWEPT_EDGE",EDGE,{"disambiguationData":[OSD([sQuery(id+"F0.wireOp",EDGE,"E0.bottom"),sQuery(id+"F0.wireOp",EDGE,"E0.left")])]});
            var Q1;
            Q1=makeQuery(id+"F2.opExtrude","SWEPT_EDGE",EDGE,{"disambiguationData":[OSD([sQuery(id+"F0.wireOp",EDGE,"E34.bottom"),sQuery(id+"F0.wireOp",EDGE,"E34.left")])]});
            var Q2;
            Q2=makeQuery(id+"F2.opExtrude","SWEPT_EDGE",EDGE,{"disambiguationData":[OSD([sQuery(id+"F0.wireOp",EDGE,"E33.bottom"),sQuery(id+"F0.wireOp",EDGE,"E33.left")])]});
            var Q3;
            Q3=makeQuery(id+"F2.opExtrude","SWEPT_EDGE",EDGE,{"disambiguationData":[OSD([sQuery(id+"F0.wireOp",EDGE,"E32.bottom"),sQuery(id+"F0.wireOp",EDGE,"E32.left")])]});
            var Q4;
            Q4=makeQuery(id+"F2.opExtrude","SWEPT_EDGE",EDGE,{"disambiguationData":[OSD([sQuery(id+"F0.wireOp",EDGE,"E35.bottom"),sQuery(id+"F0.wireOp",EDGE,"E35.left")])]});
            var Q5;
            Q5=makeQuery(id+"F2.opExtrude","SWEPT_EDGE",EDGE,{"disambiguationData":[OSD([sQuery(id+"F0.wireOp",EDGE,"E26.bottom"),sQuery(id+"F0.wireOp",EDGE,"E26.right")])]});
            var Q6;
            Q6=makeQuery(id+"F2.opExtrude","SWEPT_EDGE",EDGE,{"disambiguationData":[OSD([sQuery(id+"F0.wireOp",EDGE,"E29.bottom"),sQuery(id+"F0.wireOp",EDGE,"E29.left")])]});
            var Q7;
            Q7=makeQuery(id+"F2.opExtrude","SWEPT_EDGE",EDGE,{"disambiguationData":[OSD([sQuery(id+"F0.wireOp",EDGE,"E30.bottom"),sQuery(id+"F0.wireOp",EDGE,"E30.left")])]});
            var Q8;
            Q8=makeQuery(id+"F2.opExtrude","SWEPT_EDGE",EDGE,{"disambiguationData":[OSD([sQuery(id+"F0.wireOp",EDGE,"E31.bottom"),sQuery(id+"F0.wireOp",EDGE,"E31.left")])]});
            var Q9;
            Q9=makeQuery(id+"F2.opExtrude","SWEPT_EDGE",EDGE,{"disambiguationData":[OSD([sQuery(id+"F0.wireOp",EDGE,"E42.bottom"),sQuery(id+"F0.wireOp",EDGE,"E42.right")])]});
            var Q10;
            Q10=makeQuery(id+"F2.opExtrude","SWEPT_EDGE",EDGE,{"disambiguationData":[OSD([sQuery(id+"F0.wireOp",EDGE,"E42.bottom"),sQuery(id+"F0.wireOp",EDGE,"E42.left")])]});
            var Q11;
            Q11=makeQuery(id+"F2.opExtrude","SWEPT_EDGE",EDGE,{"disambiguationData":[OSD([sQuery(id+"F0.wireOp",EDGE,"E29.bottom"),sQuery(id+"F0.wireOp",EDGE,"E29.right")])]});
            var Q12;
            Q12=makeQuery(id+"F2.opExtrude","SWEPT_EDGE",EDGE,{"disambiguationData":[OSD([sQuery(id+"F0.wireOp",EDGE,"E26.bottom"),sQuery(id+"F0.wireOp",EDGE,"E26.left")])]});
            var Q13;
            Q13=makeQuery(id+"F2.opExtrude","SWEPT_EDGE",EDGE,{"disambiguationData":[OSD([sQuery(id+"F0.wireOp",EDGE,"E0.bottom"),sQuery(id+"F0.wireOp",EDGE,"E0.right")])]});
            var Q14;
            Q14=makeQuery(id+"F2.opExtrude","SWEPT_EDGE",EDGE,{"disambiguationData":[OSD([sQuery(id+"F0.wireOp",EDGE,"E35.bottom"),sQuery(id+"F0.wireOp",EDGE,"E35.right")])]});
            var Q15;
            Q15=makeQuery(id+"F2.opExtrude","SWEPT_EDGE",EDGE,{"disambiguationData":[OSD([sQuery(id+"F0.wireOp",EDGE,"E30.bottom"),sQuery(id+"F0.wireOp",EDGE,"E30.right")])]});
            var Q16;
            Q16=makeQuery(id+"F2.opExtrude","SWEPT_EDGE",EDGE,{"disambiguationData":[OSD([sQuery(id+"F0.wireOp",EDGE,"E31.bottom"),sQuery(id+"F0.wireOp",EDGE,"E31.right")])]});
            var Q17;
            Q17=makeQuery(id+"F2.opExtrude","SWEPT_EDGE",EDGE,{"disambiguationData":[OSD([sQuery(id+"F0.wireOp",EDGE,"E32.bottom"),sQuery(id+"F0.wireOp",EDGE,"E32.right")])]});
            var Q18;
            Q18=makeQuery(id+"F2.opExtrude","SWEPT_EDGE",EDGE,{"disambiguationData":[OSD([sQuery(id+"F0.wireOp",EDGE,"E33.bottom"),sQuery(id+"F0.wireOp",EDGE,"E33.right")])]});
            var Q19;
            Q19=makeQuery(id+"F2.opExtrude","SWEPT_EDGE",EDGE,{"disambiguationData":[OSD([sQuery(id+"F0.wireOp",EDGE,"E34.bottom"),sQuery(id+"F0.wireOp",EDGE,"E34.right")])]});
            var Q20;
            Q20=makeQuery(id+"F2.opExtrude","SWEPT_EDGE",EDGE,{"disambiguationData":[OSD([sQuery(id+"F0.wireOp",EDGE,"E34.top"),sQuery(id+"F0.wireOp",EDGE,"E34.right")])]});
            var Q21;
            Q21=makeQuery(id+"F2.opExtrude","SWEPT_EDGE",EDGE,{"disambiguationData":[OSD([sQuery(id+"F0.wireOp",EDGE,"E33.top"),sQuery(id+"F0.wireOp",EDGE,"E33.right")])]});
            var Q22;
            Q22=makeQuery(id+"F2.opExtrude","SWEPT_EDGE",EDGE,{"disambiguationData":[OSD([sQuery(id+"F0.wireOp",EDGE,"E0.right"),sQuery(id+"F0.wireOp",EDGE,"E0.top")])]});
            var Q23;
            Q23=makeQuery(id+"F2.opExtrude","SWEPT_EDGE",EDGE,{"disambiguationData":[OSD([sQuery(id+"F0.wireOp",EDGE,"E26.top"),sQuery(id+"F0.wireOp",EDGE,"E26.left")])]});
            var Q24;
            Q24=makeQuery(id+"F2.opExtrude","SWEPT_EDGE",EDGE,{"disambiguationData":[OSD([sQuery(id+"F0.wireOp",EDGE,"E35.top"),sQuery(id+"F0.wireOp",EDGE,"E35.right")])]});
            var Q25;
            Q25=makeQuery(id+"F2.opExtrude","SWEPT_EDGE",EDGE,{"disambiguationData":[OSD([sQuery(id+"F0.wireOp",EDGE,"E32.top"),sQuery(id+"F0.wireOp",EDGE,"E32.right")])]});
            var Q26;
            Q26=makeQuery(id+"F2.opExtrude","SWEPT_EDGE",EDGE,{"disambiguationData":[OSD([sQuery(id+"F0.wireOp",EDGE,"E31.top"),sQuery(id+"F0.wireOp",EDGE,"E31.right")])]});
            var Q27;
            Q27=makeQuery(id+"F2.opExtrude","SWEPT_EDGE",EDGE,{"disambiguationData":[OSD([sQuery(id+"F0.wireOp",EDGE,"E30.top"),sQuery(id+"F0.wireOp",EDGE,"E30.right")])]});
            var Q28;
            Q28=makeQuery(id+"F2.opExtrude","SWEPT_EDGE",EDGE,{"disambiguationData":[OSD([sQuery(id+"F0.wireOp",EDGE,"E29.top"),sQuery(id+"F0.wireOp",EDGE,"E29.right")])]});
            var Q29;
            Q29=makeQuery(id+"F2.opExtrude","SWEPT_EDGE",EDGE,{"disambiguationData":[OSD([sQuery(id+"F0.wireOp",EDGE,"E42.top"),sQuery(id+"F0.wireOp",EDGE,"E42.left")])]});
            var Q30;
            Q30=makeQuery(id+"F2.opExtrude","SWEPT_EDGE",EDGE,{"disambiguationData":[OSD([sQuery(id+"F0.wireOp",EDGE,"E31.top"),sQuery(id+"F0.wireOp",EDGE,"E31.left")])]});
            var Q31;
            Q31=makeQuery(id+"F2.opExtrude","SWEPT_EDGE",EDGE,{"disambiguationData":[OSD([sQuery(id+"F0.wireOp",EDGE,"E32.top"),sQuery(id+"F0.wireOp",EDGE,"E32.left")])]});
            var Q32;
            Q32=makeQuery(id+"F2.opExtrude","SWEPT_EDGE",EDGE,{"disambiguationData":[OSD([sQuery(id+"F0.wireOp",EDGE,"E33.top"),sQuery(id+"F0.wireOp",EDGE,"E33.left")])]});
            var Q33;
            Q33=makeQuery(id+"F2.opExtrude","SWEPT_EDGE",EDGE,{"disambiguationData":[OSD([sQuery(id+"F0.wireOp",EDGE,"E34.top"),sQuery(id+"F0.wireOp",EDGE,"E34.left")])]});
            var Q34;
            Q34=makeQuery(id+"F2.opExtrude","SWEPT_EDGE",EDGE,{"disambiguationData":[OSD([sQuery(id+"F0.wireOp",EDGE,"E35.top"),sQuery(id+"F0.wireOp",EDGE,"E35.left")])]});
            var Q35;
            Q35=makeQuery(id+"F2.opExtrude","SWEPT_EDGE",EDGE,{"disambiguationData":[OSD([sQuery(id+"F0.wireOp",EDGE,"E0.left"),sQuery(id+"F0.wireOp",EDGE,"E0.top")])]});
            var Q36;
            Q36=makeQuery(id+"F2.opExtrude","SWEPT_EDGE",EDGE,{"disambiguationData":[OSD([sQuery(id+"F0.wireOp",EDGE,"E26.top"),sQuery(id+"F0.wireOp",EDGE,"E26.right")])]});
            var Q37;
            Q37=makeQuery(id+"F2.opExtrude","SWEPT_EDGE",EDGE,{"disambiguationData":[OSD([sQuery(id+"F0.wireOp",EDGE,"E29.top"),sQuery(id+"F0.wireOp",EDGE,"E29.left")])]});
            var Q38;
            Q38=makeQuery(id+"F2.opExtrude","SWEPT_EDGE",EDGE,{"disambiguationData":[OSD([sQuery(id+"F0.wireOp",EDGE,"E42.top"),sQuery(id+"F0.wireOp",EDGE,"E42.right")])]});
            var Q39;
            Q39=makeQuery(id+"F2.opExtrude","SWEPT_EDGE",EDGE,{"disambiguationData":[OSD([sQuery(id+"F0.wireOp",EDGE,"E30.top"),sQuery(id+"F0.wireOp",EDGE,"E30.left")])]});
            fillet(context, id + "F5", {"entities" : qUnion([Q0, Q1, Q2, Q3, Q4, Q5, Q6, Q7, Q8, Q9, Q10, Q11, Q12, Q13, Q14, Q15, Q16, Q17, Q18, Q19, Q20, Q21, Q22, Q23, Q24, Q25, Q26, Q27, Q28, Q29, Q30, Q31, Q32, Q33, Q34, Q35, Q36, Q37, Q38, Q39]), "radius" : 2 * mm, "tangentPropagation" : true, "allowEdgeOverflow" : false});
        }
        {
            var Q0;
            Q0=makeQuery(id+"F3.opExtrude","SWEPT_EDGE",EDGE,{"disambiguationData":[OSD([sQuery(id+"F0.wireOp",EDGE,"E59.bottom"),sQuery(id+"F0.wireOp",EDGE,"E59.right")])]});
            var Q1;
            Q1=makeQuery(id+"F3.opExtrude","SWEPT_EDGE",EDGE,{"disambiguationData":[OSD([sQuery(id+"F0.wireOp",EDGE,"E60.bottom"),sQuery(id+"F0.wireOp",EDGE,"E60.left")])]});
            var Q2;
            Q2=makeQuery(id+"F3.opExtrude","SWEPT_EDGE",EDGE,{"disambiguationData":[OSD([sQuery(id+"F0.wireOp",EDGE,"E61.bottom"),sQuery(id+"F0.wireOp",EDGE,"E61.left")])]});
            var Q3;
            Q3=makeQuery(id+"F3.opExtrude","SWEPT_EDGE",EDGE,{"disambiguationData":[OSD([sQuery(id+"F0.wireOp",EDGE,"E62.top"),sQuery(id+"F0.wireOp",EDGE,"E62.right")])]});
            var Q4;
            Q4=makeQuery(id+"F3.opExtrude","SWEPT_EDGE",EDGE,{"disambiguationData":[OSD([sQuery(id+"F0.wireOp",EDGE,"E63.top"),sQuery(id+"F0.wireOp",EDGE,"E63.right")])]});
            var Q5;
            Q5=makeQuery(id+"F3.opExtrude","SWEPT_EDGE",EDGE,{"disambiguationData":[OSD([sQuery(id+"F0.wireOp",EDGE,"E62.bottom"),sQuery(id+"F0.wireOp",EDGE,"E62.left")])]});
            var Q6;
            Q6=makeQuery(id+"F3.opExtrude","SWEPT_EDGE",EDGE,{"disambiguationData":[OSD([sQuery(id+"F0.wireOp",EDGE,"E59.top"),sQuery(id+"F0.wireOp",EDGE,"E59.left")])]});
            var Q7;
            Q7=makeQuery(id+"F3.opExtrude","SWEPT_EDGE",EDGE,{"disambiguationData":[OSD([sQuery(id+"F0.wireOp",EDGE,"E63.bottom"),sQuery(id+"F0.wireOp",EDGE,"E63.left")])]});
            var Q8;
            Q8=makeQuery(id+"F3.opExtrude","SWEPT_EDGE",EDGE,{"disambiguationData":[OSD([sQuery(id+"F0.wireOp",EDGE,"E60.top"),sQuery(id+"F0.wireOp",EDGE,"E60.right")])]});
            var Q9;
            Q9=makeQuery(id+"F3.opExtrude","SWEPT_EDGE",EDGE,{"disambiguationData":[OSD([sQuery(id+"F0.wireOp",EDGE,"E61.top"),sQuery(id+"F0.wireOp",EDGE,"E61.right")])]});
            var Q10;
            Q10=makeQuery(id+"F3.opExtrude","SWEPT_EDGE",EDGE,{"disambiguationData":[OSD([sQuery(id+"F0.wireOp",EDGE,"E61.bottom"),sQuery(id+"F0.wireOp",EDGE,"E61.right")])]});
            var Q11;
            Q11=makeQuery(id+"F3.opExtrude","SWEPT_EDGE",EDGE,{"disambiguationData":[OSD([sQuery(id+"F0.wireOp",EDGE,"E60.bottom"),sQuery(id+"F0.wireOp",EDGE,"E60.right")])]});
            var Q12;
            Q12=makeQuery(id+"F3.opExtrude","SWEPT_EDGE",EDGE,{"disambiguationData":[OSD([sQuery(id+"F0.wireOp",EDGE,"E59.bottom"),sQuery(id+"F0.wireOp",EDGE,"E59.left")])]});
            var Q13;
            Q13=makeQuery(id+"F3.opExtrude","SWEPT_EDGE",EDGE,{"disambiguationData":[OSD([sQuery(id+"F0.wireOp",EDGE,"E62.top"),sQuery(id+"F0.wireOp",EDGE,"E62.left")])]});
            var Q14;
            Q14=makeQuery(id+"F3.opExtrude","SWEPT_EDGE",EDGE,{"disambiguationData":[OSD([sQuery(id+"F0.wireOp",EDGE,"E63.top"),sQuery(id+"F0.wireOp",EDGE,"E63.left")])]});
            var Q15;
            Q15=makeQuery(id+"F3.opExtrude","SWEPT_EDGE",EDGE,{"disambiguationData":[OSD([sQuery(id+"F0.wireOp",EDGE,"E59.top"),sQuery(id+"F0.wireOp",EDGE,"E59.right")])]});
            var Q16;
            Q16=makeQuery(id+"F3.opExtrude","SWEPT_EDGE",EDGE,{"disambiguationData":[OSD([sQuery(id+"F0.wireOp",EDGE,"E62.bottom"),sQuery(id+"F0.wireOp",EDGE,"E62.right")])]});
            var Q17;
            Q17=makeQuery(id+"F3.opExtrude","SWEPT_EDGE",EDGE,{"disambiguationData":[OSD([sQuery(id+"F0.wireOp",EDGE,"E63.bottom"),sQuery(id+"F0.wireOp",EDGE,"E63.right")])]});
            var Q18;
            Q18=makeQuery(id+"F3.opExtrude","SWEPT_EDGE",EDGE,{"disambiguationData":[OSD([sQuery(id+"F0.wireOp",EDGE,"E60.top"),sQuery(id+"F0.wireOp",EDGE,"E60.left")])]});
            var Q19;
            Q19=makeQuery(id+"F3.opExtrude","SWEPT_EDGE",EDGE,{"disambiguationData":[OSD([sQuery(id+"F0.wireOp",EDGE,"E61.top"),sQuery(id+"F0.wireOp",EDGE,"E61.left")])]});
            fillet(context, id + "F6", {"entities" : qUnion([Q0, Q1, Q2, Q3, Q4, Q5, Q6, Q7, Q8, Q9, Q10, Q11, Q12, Q13, Q14, Q15, Q16, Q17, Q18, Q19]), "radius" : 1 * mm, "tangentPropagation" : true, "allowEdgeOverflow" : false});
        }
        {
            var Q0;
            Q0=makeQuery(id+"F2.opExtrude","SWEPT_EDGE",EDGE,{"disambiguationData":[OSD([sQuery(id+"F0.wireOp",EDGE,"E5.top"),sQuery(id+"F0.wireOp",EDGE,"E5.right"),sQuery(id+"F0.wireOp",EDGE,"E43.bottom"),sQuery(id+"F0.wireOp",EDGE,"E43.left")])]});
            chamfer(context, id + "F7", {"entities" : qUnion([Q0]), "width" : 1 * mm, "tangentPropagation" : true});
        }
        {
            var Q0;
            Q0=makeQuery(id+"F2.opExtrude","CAP_EDGE",EDGE,{"disambiguationData":[OSD([sQuery(id+"F0.wireOp",EDGE,"E33.left")])],"isStart":false});
            var Q1;
            Q1=makeQuery(id+"F2.opExtrude","CAP_EDGE",EDGE,{"disambiguationData":[OSD([sQuery(id+"F0.wireOp",EDGE,"E34.left")])],"isStart":false});
            var Q2;
            Q2=makeQuery(id+"F2.opExtrude","CAP_EDGE",EDGE,{"disambiguationData":[OSD([sQuery(id+"F0.wireOp",EDGE,"E0.bottom")])],"isStart":false});
            var Q3;
            Q3=makeQuery(id+"F2.opExtrude","CAP_EDGE",EDGE,{"disambiguationData":[OSD([sQuery(id+"F0.wireOp",EDGE,"E26.bottom")])],"isStart":false});
            var Q4;
            Q4=makeQuery(id+"F2.opExtrude","SWEPT_FACE",FACE,{"disambiguationData":[OSD([sQuery(id+"F0.wireOp",EDGE,"E35.bottom")])]});
            var Q5;
            Q5=makeQuery(id+"F2.opExtrude","SWEPT_FACE",FACE,{"disambiguationData":[OSD([sQuery(id+"F0.wireOp",EDGE,"E32.bottom")])]});
            var Q6;
            Q6=makeQuery(id+"F2.opExtrude","CAP_EDGE",EDGE,{"disambiguationData":[OSD([sQuery(id+"F0.wireOp",EDGE,"E29.left")])],"isStart":false});
            var Q7;
            Q7=makeQuery(id+"F2.opExtrude","CAP_EDGE",EDGE,{"disambiguationData":[OSD([sQuery(id+"F0.wireOp",EDGE,"E30.bottom")])],"isStart":false});
            var Q8;
            Q8=makeQuery(id+"F2.opExtrude","CAP_EDGE",EDGE,{"disambiguationData":[OSD([sQuery(id+"F0.wireOp",EDGE,"E31.bottom")])],"isStart":false});
            var Q9;
            Q9=makeQuery(id+"F2.opExtrude","CAP_EDGE",EDGE,{"disambiguationData":[OSD([sQuery(id+"F0.wireOp",EDGE,"E42.right")])],"isStart":false});
            var Q10;
            Q10=makeQuery(id+"F2.opExtrude","CAP_EDGE",EDGE,{"disambiguationData":[OSD([sQuery(id+"F0.wireOp",EDGE,"E66"),sQuery(id+"F0.wireOp",EDGE,"E67")])],"isStart":false});
            var Q11;
            {var subQ0=sQuery(id+"F0.wireOp",EDGE,"E68");var subQ1=sQuery(id+"F0.wireOp",EDGE,"E67");Q11=makeQuery(id+"F4.opChamfer","BLEND_EDGE",EDGE,{"blendedFrom":[makeQuery(id+"F2.boolean.opBoolean","MERGE",EDGE,{"derivedFrom":[makeQuery(id+"F1.opExtrude","SWEPT_EDGE",EDGE,{"disambiguationData":[OSD([subQ1,subQ0])]}),makeQuery(id+"F2.opExtrude","SWEPT_EDGE",EDGE,{"disambiguationData":[OSD([subQ1,subQ0])]})]}),makeQuery(id+"F2.opExtrude","CAP_FACE",FACE,{"disambiguationData":[OSD([sQuery(id+"F0.wireOp",EDGE,"E0.bottom"),sQuery(id+"F0.wireOp",EDGE,"E0.left"),sQuery(id+"F0.wireOp",EDGE,"E0.right"),sQuery(id+"F0.wireOp",EDGE,"E0.top"),sQuery(id+"F0.wireOp",EDGE,"E26.bottom"),sQuery(id+"F0.wireOp",EDGE,"E26.top"),sQuery(id+"F0.wireOp",EDGE,"E26.left"),sQuery(id+"F0.wireOp",EDGE,"E26.right"),sQuery(id+"F0.wireOp",EDGE,"E29.bottom"),sQuery(id+"F0.wireOp",EDGE,"E29.top"),sQuery(id+"F0.wireOp",EDGE,"E29.left"),sQuery(id+"F0.wireOp",EDGE,"E29.right"),sQuery(id+"F0.wireOp",EDGE,"E30.bottom"),sQuery(id+"F0.wireOp",EDGE,"E30.top"),sQuery(id+"F0.wireOp",EDGE,"E30.left"),sQuery(id+"F0.wireOp",EDGE,"E30.right"),sQuery(id+"F0.wireOp",EDGE,"E31.bottom"),sQuery(id+"F0.wireOp",EDGE,"E31.top"),sQuery(id+"F0.wireOp",EDGE,"E31.left"),sQuery(id+"F0.wireOp",EDGE,"E31.right"),sQuery(id+"F0.wireOp",EDGE,"E32.bottom"),sQuery(id+"F0.wireOp",EDGE,"E32.top"),sQuery(id+"F0.wireOp",EDGE,"E32.left"),sQuery(id+"F0.wireOp",EDGE,"E32.right"),sQuery(id+"F0.wireOp",EDGE,"E33.bottom"),sQuery(id+"F0.wireOp",EDGE,"E33.top"),sQuery(id+"F0.wireOp",EDGE,"E33.left"),sQuery(id+"F0.wireOp",EDGE,"E33.right"),sQuery(id+"F0.wireOp",EDGE,"E34.bottom"),sQuery(id+"F0.wireOp",EDGE,"E34.top"),sQuery(id+"F0.wireOp",EDGE,"E34.left"),sQuery(id+"F0.wireOp",EDGE,"E34.right"),sQuery(id+"F0.wireOp",EDGE,"E35.bottom"),sQuery(id+"F0.wireOp",EDGE,"E35.top"),sQuery(id+"F0.wireOp",EDGE,"E35.left"),sQuery(id+"F0.wireOp",EDGE,"E35.right"),sQuery(id+"F0.wireOp",EDGE,"E42.bottom"),sQuery(id+"F0.wireOp",EDGE,"E42.top"),sQuery(id+"F0.wireOp",EDGE,"E42.left"),sQuery(id+"F0.wireOp",EDGE,"E42.right"),sQuery(id+"F0.wireOp",EDGE,"E43.bottom"),sQuery(id+"F0.wireOp",EDGE,"E43.left"),sQuery(id+"F0.wireOp",EDGE,"E44.left"),sQuery(id+"F0.wireOp",EDGE,"E45.left"),sQuery(id+"F0.wireOp",EDGE,"E47.bottom"),sQuery(id+"F0.wireOp",EDGE,"E64"),sQuery(id+"F0.wireOp",EDGE,"E65"),sQuery(id+"F0.wireOp",EDGE,"E66"),subQ1,subQ0,sQuery(id+"F0.wireOp",EDGE,"E69"),sQuery(id+"F0.wireOp",EDGE,"E70"),sQuery(id+"F0.wireOp",EDGE,"E71"),sQuery(id+"F0.wireOp",EDGE,"E72"),sQuery(id+"F0.wireOp",EDGE,"E79"),sQuery(id+"F0.wireOp",EDGE,"E81")])],"isStart":false})],"blendedInto":[makeQuery(id+"F2.opExtrude","CAP_FACE",FACE,{"disambiguationData":[OSD([sQuery(id+"F0.wireOp",EDGE,"E0.bottom"),sQuery(id+"F0.wireOp",EDGE,"E0.left"),sQuery(id+"F0.wireOp",EDGE,"E0.right"),sQuery(id+"F0.wireOp",EDGE,"E0.top"),sQuery(id+"F0.wireOp",EDGE,"E26.bottom"),sQuery(id+"F0.wireOp",EDGE,"E26.top"),sQuery(id+"F0.wireOp",EDGE,"E26.left"),sQuery(id+"F0.wireOp",EDGE,"E26.right"),sQuery(id+"F0.wireOp",EDGE,"E29.bottom"),sQuery(id+"F0.wireOp",EDGE,"E29.top"),sQuery(id+"F0.wireOp",EDGE,"E29.left"),sQuery(id+"F0.wireOp",EDGE,"E29.right"),sQuery(id+"F0.wireOp",EDGE,"E30.bottom"),sQuery(id+"F0.wireOp",EDGE,"E30.top"),sQuery(id+"F0.wireOp",EDGE,"E30.left"),sQuery(id+"F0.wireOp",EDGE,"E30.right"),sQuery(id+"F0.wireOp",EDGE,"E31.bottom"),sQuery(id+"F0.wireOp",EDGE,"E31.top"),sQuery(id+"F0.wireOp",EDGE,"E31.left"),sQuery(id+"F0.wireOp",EDGE,"E31.right"),sQuery(id+"F0.wireOp",EDGE,"E32.bottom"),sQuery(id+"F0.wireOp",EDGE,"E32.top"),sQuery(id+"F0.wireOp",EDGE,"E32.left"),sQuery(id+"F0.wireOp",EDGE,"E32.right"),sQuery(id+"F0.wireOp",EDGE,"E33.bottom"),sQuery(id+"F0.wireOp",EDGE,"E33.top"),sQuery(id+"F0.wireOp",EDGE,"E33.left"),sQuery(id+"F0.wireOp",EDGE,"E33.right"),sQuery(id+"F0.wireOp",EDGE,"E34.bottom"),sQuery(id+"F0.wireOp",EDGE,"E34.top"),sQuery(id+"F0.wireOp",EDGE,"E34.left"),sQuery(id+"F0.wireOp",EDGE,"E34.right"),sQuery(id+"F0.wireOp",EDGE,"E35.bottom"),sQuery(id+"F0.wireOp",EDGE,"E35.top"),sQuery(id+"F0.wireOp",EDGE,"E35.left"),sQuery(id+"F0.wireOp",EDGE,"E35.right"),sQuery(id+"F0.wireOp",EDGE,"E42.bottom"),sQuery(id+"F0.wireOp",EDGE,"E42.top"),sQuery(id+"F0.wireOp",EDGE,"E42.left"),sQuery(id+"F0.wireOp",EDGE,"E42.right"),sQuery(id+"F0.wireOp",EDGE,"E43.bottom"),sQuery(id+"F0.wireOp",EDGE,"E43.left"),sQuery(id+"F0.wireOp",EDGE,"E44.left"),sQuery(id+"F0.wireOp",EDGE,"E45.left"),sQuery(id+"F0.wireOp",EDGE,"E47.bottom"),sQuery(id+"F0.wireOp",EDGE,"E64"),sQuery(id+"F0.wireOp",EDGE,"E65"),sQuery(id+"F0.wireOp",EDGE,"E66"),subQ1,subQ0,sQuery(id+"F0.wireOp",EDGE,"E69"),sQuery(id+"F0.wireOp",EDGE,"E70"),sQuery(id+"F0.wireOp",EDGE,"E71"),sQuery(id+"F0.wireOp",EDGE,"E72"),sQuery(id+"F0.wireOp",EDGE,"E79"),sQuery(id+"F0.wireOp",EDGE,"E81")])],"isStart":false})]});}
            var Q12;
            Q12=makeQuery(id+"F2.opExtrude","CAP_EDGE",EDGE,{"disambiguationData":[OSD([sQuery(id+"F0.wireOp",EDGE,"E68")])],"isStart":false});
            var Q13;
            Q13=makeQuery(id+"F2.opExtrude","CAP_EDGE",EDGE,{"disambiguationData":[OSD([sQuery(id+"F0.wireOp",EDGE,"E43.left"),sQuery(id+"F0.wireOp",EDGE,"E44.left"),sQuery(id+"F0.wireOp",EDGE,"E45.left")])],"isStart":false});
            var Q14;
            Q14=makeQuery(id+"F2.opExtrude","CAP_EDGE",EDGE,{"disambiguationData":[OSD([sQuery(id+"F0.wireOp",EDGE,"E79")])],"isStart":false});
            var Q15;
            {var subQ0=sQuery(id+"F0.wireOp",EDGE,"E43.left");var subQ1=sQuery(id+"F0.wireOp",EDGE,"E43.bottom");Q15=makeQuery(id+"F7.opChamfer","BLEND_EDGE",EDGE,{"blendedFrom":[makeQuery(id+"F2.opExtrude","SWEPT_EDGE",EDGE,{"disambiguationData":[OSD([sQuery(id+"F0.wireOp",EDGE,"E5.top"),sQuery(id+"F0.wireOp",EDGE,"E5.right"),subQ1,subQ0])]}),makeQuery(id+"F2.opExtrude","CAP_FACE",FACE,{"disambiguationData":[OSD([sQuery(id+"F0.wireOp",EDGE,"E0.bottom"),sQuery(id+"F0.wireOp",EDGE,"E0.left"),sQuery(id+"F0.wireOp",EDGE,"E0.right"),sQuery(id+"F0.wireOp",EDGE,"E0.top"),sQuery(id+"F0.wireOp",EDGE,"E26.bottom"),sQuery(id+"F0.wireOp",EDGE,"E26.top"),sQuery(id+"F0.wireOp",EDGE,"E26.left"),sQuery(id+"F0.wireOp",EDGE,"E26.right"),sQuery(id+"F0.wireOp",EDGE,"E29.bottom"),sQuery(id+"F0.wireOp",EDGE,"E29.top"),sQuery(id+"F0.wireOp",EDGE,"E29.left"),sQuery(id+"F0.wireOp",EDGE,"E29.right"),sQuery(id+"F0.wireOp",EDGE,"E30.bottom"),sQuery(id+"F0.wireOp",EDGE,"E30.top"),sQuery(id+"F0.wireOp",EDGE,"E30.left"),sQuery(id+"F0.wireOp",EDGE,"E30.right"),sQuery(id+"F0.wireOp",EDGE,"E31.bottom"),sQuery(id+"F0.wireOp",EDGE,"E31.top"),sQuery(id+"F0.wireOp",EDGE,"E31.left"),sQuery(id+"F0.wireOp",EDGE,"E31.right"),sQuery(id+"F0.wireOp",EDGE,"E32.bottom"),sQuery(id+"F0.wireOp",EDGE,"E32.top"),sQuery(id+"F0.wireOp",EDGE,"E32.left"),sQuery(id+"F0.wireOp",EDGE,"E32.right"),sQuery(id+"F0.wireOp",EDGE,"E33.bottom"),sQuery(id+"F0.wireOp",EDGE,"E33.top"),sQuery(id+"F0.wireOp",EDGE,"E33.left"),sQuery(id+"F0.wireOp",EDGE,"E33.right"),sQuery(id+"F0.wireOp",EDGE,"E34.bottom"),sQuery(id+"F0.wireOp",EDGE,"E34.top"),sQuery(id+"F0.wireOp",EDGE,"E34.left"),sQuery(id+"F0.wireOp",EDGE,"E34.right"),sQuery(id+"F0.wireOp",EDGE,"E35.bottom"),sQuery(id+"F0.wireOp",EDGE,"E35.top"),sQuery(id+"F0.wireOp",EDGE,"E35.left"),sQuery(id+"F0.wireOp",EDGE,"E35.right"),sQuery(id+"F0.wireOp",EDGE,"E42.bottom"),sQuery(id+"F0.wireOp",EDGE,"E42.top"),sQuery(id+"F0.wireOp",EDGE,"E42.left"),sQuery(id+"F0.wireOp",EDGE,"E42.right"),subQ1,subQ0,sQuery(id+"F0.wireOp",EDGE,"E44.left"),sQuery(id+"F0.wireOp",EDGE,"E45.left"),sQuery(id+"F0.wireOp",EDGE,"E47.bottom"),sQuery(id+"F0.wireOp",EDGE,"E64"),sQuery(id+"F0.wireOp",EDGE,"E65"),sQuery(id+"F0.wireOp",EDGE,"E66"),sQuery(id+"F0.wireOp",EDGE,"E67"),sQuery(id+"F0.wireOp",EDGE,"E68"),sQuery(id+"F0.wireOp",EDGE,"E69"),sQuery(id+"F0.wireOp",EDGE,"E70"),sQuery(id+"F0.wireOp",EDGE,"E71"),sQuery(id+"F0.wireOp",EDGE,"E72"),sQuery(id+"F0.wireOp",EDGE,"E79"),sQuery(id+"F0.wireOp",EDGE,"E81")])],"isStart":false})],"blendedInto":[makeQuery(id+"F2.opExtrude","CAP_FACE",FACE,{"disambiguationData":[OSD([sQuery(id+"F0.wireOp",EDGE,"E0.bottom"),sQuery(id+"F0.wireOp",EDGE,"E0.left"),sQuery(id+"F0.wireOp",EDGE,"E0.right"),sQuery(id+"F0.wireOp",EDGE,"E0.top"),sQuery(id+"F0.wireOp",EDGE,"E26.bottom"),sQuery(id+"F0.wireOp",EDGE,"E26.top"),sQuery(id+"F0.wireOp",EDGE,"E26.left"),sQuery(id+"F0.wireOp",EDGE,"E26.right"),sQuery(id+"F0.wireOp",EDGE,"E29.bottom"),sQuery(id+"F0.wireOp",EDGE,"E29.top"),sQuery(id+"F0.wireOp",EDGE,"E29.left"),sQuery(id+"F0.wireOp",EDGE,"E29.right"),sQuery(id+"F0.wireOp",EDGE,"E30.bottom"),sQuery(id+"F0.wireOp",EDGE,"E30.top"),sQuery(id+"F0.wireOp",EDGE,"E30.left"),sQuery(id+"F0.wireOp",EDGE,"E30.right"),sQuery(id+"F0.wireOp",EDGE,"E31.bottom"),sQuery(id+"F0.wireOp",EDGE,"E31.top"),sQuery(id+"F0.wireOp",EDGE,"E31.left"),sQuery(id+"F0.wireOp",EDGE,"E31.right"),sQuery(id+"F0.wireOp",EDGE,"E32.bottom"),sQuery(id+"F0.wireOp",EDGE,"E32.top"),sQuery(id+"F0.wireOp",EDGE,"E32.left"),sQuery(id+"F0.wireOp",EDGE,"E32.right"),sQuery(id+"F0.wireOp",EDGE,"E33.bottom"),sQuery(id+"F0.wireOp",EDGE,"E33.top"),sQuery(id+"F0.wireOp",EDGE,"E33.left"),sQuery(id+"F0.wireOp",EDGE,"E33.right"),sQuery(id+"F0.wireOp",EDGE,"E34.bottom"),sQuery(id+"F0.wireOp",EDGE,"E34.top"),sQuery(id+"F0.wireOp",EDGE,"E34.left"),sQuery(id+"F0.wireOp",EDGE,"E34.right"),sQuery(id+"F0.wireOp",EDGE,"E35.bottom"),sQuery(id+"F0.wireOp",EDGE,"E35.top"),sQuery(id+"F0.wireOp",EDGE,"E35.left"),sQuery(id+"F0.wireOp",EDGE,"E35.right"),sQuery(id+"F0.wireOp",EDGE,"E42.bottom"),sQuery(id+"F0.wireOp",EDGE,"E42.top"),sQuery(id+"F0.wireOp",EDGE,"E42.left"),sQuery(id+"F0.wireOp",EDGE,"E42.right"),subQ1,subQ0,sQuery(id+"F0.wireOp",EDGE,"E44.left"),sQuery(id+"F0.wireOp",EDGE,"E45.left"),sQuery(id+"F0.wireOp",EDGE,"E47.bottom"),sQuery(id+"F0.wireOp",EDGE,"E64"),sQuery(id+"F0.wireOp",EDGE,"E65"),sQuery(id+"F0.wireOp",EDGE,"E66"),sQuery(id+"F0.wireOp",EDGE,"E67"),sQuery(id+"F0.wireOp",EDGE,"E68"),sQuery(id+"F0.wireOp",EDGE,"E69"),sQuery(id+"F0.wireOp",EDGE,"E70"),sQuery(id+"F0.wireOp",EDGE,"E71"),sQuery(id+"F0.wireOp",EDGE,"E72"),sQuery(id+"F0.wireOp",EDGE,"E79"),sQuery(id+"F0.wireOp",EDGE,"E81")])],"isStart":false})]});}
            var Q16;
            Q16=makeQuery(id+"F2.opExtrude","CAP_EDGE",EDGE,{"disambiguationData":[OSD([sQuery(id+"F0.wireOp",EDGE,"E43.bottom"),sQuery(id+"F0.wireOp",EDGE,"E47.bottom")])],"isStart":false});
            var Q17;
            Q17=makeQuery(id+"F2.opExtrude","CAP_EDGE",EDGE,{"disambiguationData":[OSD([sQuery(id+"F0.wireOp",EDGE,"E81")])],"isStart":false});
            var Q18;
            Q18=makeQuery(id+"F2.opExtrude","CAP_EDGE",EDGE,{"disambiguationData":[OSD([sQuery(id+"F0.wireOp",EDGE,"E72")])],"isStart":false});
            var Q19;
            Q19=makeQuery(id+"F2.opExtrude","CAP_EDGE",EDGE,{"disambiguationData":[OSD([sQuery(id+"F0.wireOp",EDGE,"E64"),sQuery(id+"F0.wireOp",EDGE,"E65"),sQuery(id+"F0.wireOp",EDGE,"E69")])],"isStart":false});
            var Q20;
            {var subQ0=sQuery(id+"F0.wireOp",EDGE,"E66");var subQ1=sQuery(id+"F0.wireOp",EDGE,"E65");Q20=makeQuery(id+"F4.opChamfer","BLEND_EDGE",EDGE,{"blendedFrom":[makeQuery(id+"F2.boolean.opBoolean","MERGE",EDGE,{"derivedFrom":[makeQuery(id+"F1.opExtrude","SWEPT_EDGE",EDGE,{"disambiguationData":[OSD([subQ1,subQ0])]}),makeQuery(id+"F2.opExtrude","SWEPT_EDGE",EDGE,{"disambiguationData":[OSD([subQ1,subQ0])]})]}),makeQuery(id+"F2.opExtrude","CAP_FACE",FACE,{"disambiguationData":[OSD([sQuery(id+"F0.wireOp",EDGE,"E0.bottom"),sQuery(id+"F0.wireOp",EDGE,"E0.left"),sQuery(id+"F0.wireOp",EDGE,"E0.right"),sQuery(id+"F0.wireOp",EDGE,"E0.top"),sQuery(id+"F0.wireOp",EDGE,"E26.bottom"),sQuery(id+"F0.wireOp",EDGE,"E26.top"),sQuery(id+"F0.wireOp",EDGE,"E26.left"),sQuery(id+"F0.wireOp",EDGE,"E26.right"),sQuery(id+"F0.wireOp",EDGE,"E29.bottom"),sQuery(id+"F0.wireOp",EDGE,"E29.top"),sQuery(id+"F0.wireOp",EDGE,"E29.left"),sQuery(id+"F0.wireOp",EDGE,"E29.right"),sQuery(id+"F0.wireOp",EDGE,"E30.bottom"),sQuery(id+"F0.wireOp",EDGE,"E30.top"),sQuery(id+"F0.wireOp",EDGE,"E30.left"),sQuery(id+"F0.wireOp",EDGE,"E30.right"),sQuery(id+"F0.wireOp",EDGE,"E31.bottom"),sQuery(id+"F0.wireOp",EDGE,"E31.top"),sQuery(id+"F0.wireOp",EDGE,"E31.left"),sQuery(id+"F0.wireOp",EDGE,"E31.right"),sQuery(id+"F0.wireOp",EDGE,"E32.bottom"),sQuery(id+"F0.wireOp",EDGE,"E32.top"),sQuery(id+"F0.wireOp",EDGE,"E32.left"),sQuery(id+"F0.wireOp",EDGE,"E32.right"),sQuery(id+"F0.wireOp",EDGE,"E33.bottom"),sQuery(id+"F0.wireOp",EDGE,"E33.top"),sQuery(id+"F0.wireOp",EDGE,"E33.left"),sQuery(id+"F0.wireOp",EDGE,"E33.right"),sQuery(id+"F0.wireOp",EDGE,"E34.bottom"),sQuery(id+"F0.wireOp",EDGE,"E34.top"),sQuery(id+"F0.wireOp",EDGE,"E34.left"),sQuery(id+"F0.wireOp",EDGE,"E34.right"),sQuery(id+"F0.wireOp",EDGE,"E35.bottom"),sQuery(id+"F0.wireOp",EDGE,"E35.top"),sQuery(id+"F0.wireOp",EDGE,"E35.left"),sQuery(id+"F0.wireOp",EDGE,"E35.right"),sQuery(id+"F0.wireOp",EDGE,"E42.bottom"),sQuery(id+"F0.wireOp",EDGE,"E42.top"),sQuery(id+"F0.wireOp",EDGE,"E42.left"),sQuery(id+"F0.wireOp",EDGE,"E42.right"),sQuery(id+"F0.wireOp",EDGE,"E43.bottom"),sQuery(id+"F0.wireOp",EDGE,"E43.left"),sQuery(id+"F0.wireOp",EDGE,"E44.left"),sQuery(id+"F0.wireOp",EDGE,"E45.left"),sQuery(id+"F0.wireOp",EDGE,"E47.bottom"),sQuery(id+"F0.wireOp",EDGE,"E64"),subQ1,subQ0,sQuery(id+"F0.wireOp",EDGE,"E67"),sQuery(id+"F0.wireOp",EDGE,"E68"),sQuery(id+"F0.wireOp",EDGE,"E69"),sQuery(id+"F0.wireOp",EDGE,"E70"),sQuery(id+"F0.wireOp",EDGE,"E71"),sQuery(id+"F0.wireOp",EDGE,"E72"),sQuery(id+"F0.wireOp",EDGE,"E79"),sQuery(id+"F0.wireOp",EDGE,"E81")])],"isStart":false})],"blendedInto":[makeQuery(id+"F2.opExtrude","CAP_FACE",FACE,{"disambiguationData":[OSD([sQuery(id+"F0.wireOp",EDGE,"E0.bottom"),sQuery(id+"F0.wireOp",EDGE,"E0.left"),sQuery(id+"F0.wireOp",EDGE,"E0.right"),sQuery(id+"F0.wireOp",EDGE,"E0.top"),sQuery(id+"F0.wireOp",EDGE,"E26.bottom"),sQuery(id+"F0.wireOp",EDGE,"E26.top"),sQuery(id+"F0.wireOp",EDGE,"E26.left"),sQuery(id+"F0.wireOp",EDGE,"E26.right"),sQuery(id+"F0.wireOp",EDGE,"E29.bottom"),sQuery(id+"F0.wireOp",EDGE,"E29.top"),sQuery(id+"F0.wireOp",EDGE,"E29.left"),sQuery(id+"F0.wireOp",EDGE,"E29.right"),sQuery(id+"F0.wireOp",EDGE,"E30.bottom"),sQuery(id+"F0.wireOp",EDGE,"E30.top"),sQuery(id+"F0.wireOp",EDGE,"E30.left"),sQuery(id+"F0.wireOp",EDGE,"E30.right"),sQuery(id+"F0.wireOp",EDGE,"E31.bottom"),sQuery(id+"F0.wireOp",EDGE,"E31.top"),sQuery(id+"F0.wireOp",EDGE,"E31.left"),sQuery(id+"F0.wireOp",EDGE,"E31.right"),sQuery(id+"F0.wireOp",EDGE,"E32.bottom"),sQuery(id+"F0.wireOp",EDGE,"E32.top"),sQuery(id+"F0.wireOp",EDGE,"E32.left"),sQuery(id+"F0.wireOp",EDGE,"E32.right"),sQuery(id+"F0.wireOp",EDGE,"E33.bottom"),sQuery(id+"F0.wireOp",EDGE,"E33.top"),sQuery(id+"F0.wireOp",EDGE,"E33.left"),sQuery(id+"F0.wireOp",EDGE,"E33.right"),sQuery(id+"F0.wireOp",EDGE,"E34.bottom"),sQuery(id+"F0.wireOp",EDGE,"E34.top"),sQuery(id+"F0.wireOp",EDGE,"E34.left"),sQuery(id+"F0.wireOp",EDGE,"E34.right"),sQuery(id+"F0.wireOp",EDGE,"E35.bottom"),sQuery(id+"F0.wireOp",EDGE,"E35.top"),sQuery(id+"F0.wireOp",EDGE,"E35.left"),sQuery(id+"F0.wireOp",EDGE,"E35.right"),sQuery(id+"F0.wireOp",EDGE,"E42.bottom"),sQuery(id+"F0.wireOp",EDGE,"E42.top"),sQuery(id+"F0.wireOp",EDGE,"E42.left"),sQuery(id+"F0.wireOp",EDGE,"E42.right"),sQuery(id+"F0.wireOp",EDGE,"E43.bottom"),sQuery(id+"F0.wireOp",EDGE,"E43.left"),sQuery(id+"F0.wireOp",EDGE,"E44.left"),sQuery(id+"F0.wireOp",EDGE,"E45.left"),sQuery(id+"F0.wireOp",EDGE,"E47.bottom"),sQuery(id+"F0.wireOp",EDGE,"E64"),subQ1,subQ0,sQuery(id+"F0.wireOp",EDGE,"E67"),sQuery(id+"F0.wireOp",EDGE,"E68"),sQuery(id+"F0.wireOp",EDGE,"E69"),sQuery(id+"F0.wireOp",EDGE,"E70"),sQuery(id+"F0.wireOp",EDGE,"E71"),sQuery(id+"F0.wireOp",EDGE,"E72"),sQuery(id+"F0.wireOp",EDGE,"E79"),sQuery(id+"F0.wireOp",EDGE,"E81")])],"isStart":false})]});}
            var Q21;
            {var subQ0=sQuery(id+"F0.wireOp",EDGE,"E72");var subQ1=sQuery(id+"F0.wireOp",EDGE,"E71");Q21=makeQuery(id+"F4.opChamfer","BLEND_EDGE",EDGE,{"blendedFrom":[makeQuery(id+"F2.boolean.opBoolean","MERGE",EDGE,{"derivedFrom":[makeQuery(id+"F1.opExtrude","SWEPT_EDGE",EDGE,{"disambiguationData":[OSD([subQ1,subQ0])]}),makeQuery(id+"F2.opExtrude","SWEPT_EDGE",EDGE,{"disambiguationData":[OSD([subQ1,subQ0])]})]}),makeQuery(id+"F2.opExtrude","CAP_FACE",FACE,{"disambiguationData":[OSD([sQuery(id+"F0.wireOp",EDGE,"E0.bottom"),sQuery(id+"F0.wireOp",EDGE,"E0.left"),sQuery(id+"F0.wireOp",EDGE,"E0.right"),sQuery(id+"F0.wireOp",EDGE,"E0.top"),sQuery(id+"F0.wireOp",EDGE,"E26.bottom"),sQuery(id+"F0.wireOp",EDGE,"E26.top"),sQuery(id+"F0.wireOp",EDGE,"E26.left"),sQuery(id+"F0.wireOp",EDGE,"E26.right"),sQuery(id+"F0.wireOp",EDGE,"E29.bottom"),sQuery(id+"F0.wireOp",EDGE,"E29.top"),sQuery(id+"F0.wireOp",EDGE,"E29.left"),sQuery(id+"F0.wireOp",EDGE,"E29.right"),sQuery(id+"F0.wireOp",EDGE,"E30.bottom"),sQuery(id+"F0.wireOp",EDGE,"E30.top"),sQuery(id+"F0.wireOp",EDGE,"E30.left"),sQuery(id+"F0.wireOp",EDGE,"E30.right"),sQuery(id+"F0.wireOp",EDGE,"E31.bottom"),sQuery(id+"F0.wireOp",EDGE,"E31.top"),sQuery(id+"F0.wireOp",EDGE,"E31.left"),sQuery(id+"F0.wireOp",EDGE,"E31.right"),sQuery(id+"F0.wireOp",EDGE,"E32.bottom"),sQuery(id+"F0.wireOp",EDGE,"E32.top"),sQuery(id+"F0.wireOp",EDGE,"E32.left"),sQuery(id+"F0.wireOp",EDGE,"E32.right"),sQuery(id+"F0.wireOp",EDGE,"E33.bottom"),sQuery(id+"F0.wireOp",EDGE,"E33.top"),sQuery(id+"F0.wireOp",EDGE,"E33.left"),sQuery(id+"F0.wireOp",EDGE,"E33.right"),sQuery(id+"F0.wireOp",EDGE,"E34.bottom"),sQuery(id+"F0.wireOp",EDGE,"E34.top"),sQuery(id+"F0.wireOp",EDGE,"E34.left"),sQuery(id+"F0.wireOp",EDGE,"E34.right"),sQuery(id+"F0.wireOp",EDGE,"E35.bottom"),sQuery(id+"F0.wireOp",EDGE,"E35.top"),sQuery(id+"F0.wireOp",EDGE,"E35.left"),sQuery(id+"F0.wireOp",EDGE,"E35.right"),sQuery(id+"F0.wireOp",EDGE,"E42.bottom"),sQuery(id+"F0.wireOp",EDGE,"E42.top"),sQuery(id+"F0.wireOp",EDGE,"E42.left"),sQuery(id+"F0.wireOp",EDGE,"E42.right"),sQuery(id+"F0.wireOp",EDGE,"E43.bottom"),sQuery(id+"F0.wireOp",EDGE,"E43.left"),sQuery(id+"F0.wireOp",EDGE,"E44.left"),sQuery(id+"F0.wireOp",EDGE,"E45.left"),sQuery(id+"F0.wireOp",EDGE,"E47.bottom"),sQuery(id+"F0.wireOp",EDGE,"E64"),sQuery(id+"F0.wireOp",EDGE,"E65"),sQuery(id+"F0.wireOp",EDGE,"E66"),sQuery(id+"F0.wireOp",EDGE,"E67"),sQuery(id+"F0.wireOp",EDGE,"E68"),sQuery(id+"F0.wireOp",EDGE,"E69"),sQuery(id+"F0.wireOp",EDGE,"E70"),subQ1,subQ0,sQuery(id+"F0.wireOp",EDGE,"E79"),sQuery(id+"F0.wireOp",EDGE,"E81")])],"isStart":false})],"blendedInto":[makeQuery(id+"F2.opExtrude","CAP_FACE",FACE,{"disambiguationData":[OSD([sQuery(id+"F0.wireOp",EDGE,"E0.bottom"),sQuery(id+"F0.wireOp",EDGE,"E0.left"),sQuery(id+"F0.wireOp",EDGE,"E0.right"),sQuery(id+"F0.wireOp",EDGE,"E0.top"),sQuery(id+"F0.wireOp",EDGE,"E26.bottom"),sQuery(id+"F0.wireOp",EDGE,"E26.top"),sQuery(id+"F0.wireOp",EDGE,"E26.left"),sQuery(id+"F0.wireOp",EDGE,"E26.right"),sQuery(id+"F0.wireOp",EDGE,"E29.bottom"),sQuery(id+"F0.wireOp",EDGE,"E29.top"),sQuery(id+"F0.wireOp",EDGE,"E29.left"),sQuery(id+"F0.wireOp",EDGE,"E29.right"),sQuery(id+"F0.wireOp",EDGE,"E30.bottom"),sQuery(id+"F0.wireOp",EDGE,"E30.top"),sQuery(id+"F0.wireOp",EDGE,"E30.left"),sQuery(id+"F0.wireOp",EDGE,"E30.right"),sQuery(id+"F0.wireOp",EDGE,"E31.bottom"),sQuery(id+"F0.wireOp",EDGE,"E31.top"),sQuery(id+"F0.wireOp",EDGE,"E31.left"),sQuery(id+"F0.wireOp",EDGE,"E31.right"),sQuery(id+"F0.wireOp",EDGE,"E32.bottom"),sQuery(id+"F0.wireOp",EDGE,"E32.top"),sQuery(id+"F0.wireOp",EDGE,"E32.left"),sQuery(id+"F0.wireOp",EDGE,"E32.right"),sQuery(id+"F0.wireOp",EDGE,"E33.bottom"),sQuery(id+"F0.wireOp",EDGE,"E33.top"),sQuery(id+"F0.wireOp",EDGE,"E33.left"),sQuery(id+"F0.wireOp",EDGE,"E33.right"),sQuery(id+"F0.wireOp",EDGE,"E34.bottom"),sQuery(id+"F0.wireOp",EDGE,"E34.top"),sQuery(id+"F0.wireOp",EDGE,"E34.left"),sQuery(id+"F0.wireOp",EDGE,"E34.right"),sQuery(id+"F0.wireOp",EDGE,"E35.bottom"),sQuery(id+"F0.wireOp",EDGE,"E35.top"),sQuery(id+"F0.wireOp",EDGE,"E35.left"),sQuery(id+"F0.wireOp",EDGE,"E35.right"),sQuery(id+"F0.wireOp",EDGE,"E42.bottom"),sQuery(id+"F0.wireOp",EDGE,"E42.top"),sQuery(id+"F0.wireOp",EDGE,"E42.left"),sQuery(id+"F0.wireOp",EDGE,"E42.right"),sQuery(id+"F0.wireOp",EDGE,"E43.bottom"),sQuery(id+"F0.wireOp",EDGE,"E43.left"),sQuery(id+"F0.wireOp",EDGE,"E44.left"),sQuery(id+"F0.wireOp",EDGE,"E45.left"),sQuery(id+"F0.wireOp",EDGE,"E47.bottom"),sQuery(id+"F0.wireOp",EDGE,"E64"),sQuery(id+"F0.wireOp",EDGE,"E65"),sQuery(id+"F0.wireOp",EDGE,"E66"),sQuery(id+"F0.wireOp",EDGE,"E67"),sQuery(id+"F0.wireOp",EDGE,"E68"),sQuery(id+"F0.wireOp",EDGE,"E69"),sQuery(id+"F0.wireOp",EDGE,"E70"),subQ1,subQ0,sQuery(id+"F0.wireOp",EDGE,"E79"),sQuery(id+"F0.wireOp",EDGE,"E81")])],"isStart":false})]});}
            var Q22;
            {var subQ0=sQuery(id+"F0.wireOp",EDGE,"E70");var subQ1=sQuery(id+"F0.wireOp",EDGE,"E69");Q22=makeQuery(id+"F4.opChamfer","BLEND_EDGE",EDGE,{"blendedFrom":[makeQuery(id+"F2.boolean.opBoolean","MERGE",EDGE,{"derivedFrom":[makeQuery(id+"F1.opExtrude","SWEPT_EDGE",EDGE,{"disambiguationData":[OSD([subQ1,subQ0])]}),makeQuery(id+"F2.opExtrude","SWEPT_EDGE",EDGE,{"disambiguationData":[OSD([subQ1,subQ0])]})]}),makeQuery(id+"F2.opExtrude","CAP_FACE",FACE,{"disambiguationData":[OSD([sQuery(id+"F0.wireOp",EDGE,"E0.bottom"),sQuery(id+"F0.wireOp",EDGE,"E0.left"),sQuery(id+"F0.wireOp",EDGE,"E0.right"),sQuery(id+"F0.wireOp",EDGE,"E0.top"),sQuery(id+"F0.wireOp",EDGE,"E26.bottom"),sQuery(id+"F0.wireOp",EDGE,"E26.top"),sQuery(id+"F0.wireOp",EDGE,"E26.left"),sQuery(id+"F0.wireOp",EDGE,"E26.right"),sQuery(id+"F0.wireOp",EDGE,"E29.bottom"),sQuery(id+"F0.wireOp",EDGE,"E29.top"),sQuery(id+"F0.wireOp",EDGE,"E29.left"),sQuery(id+"F0.wireOp",EDGE,"E29.right"),sQuery(id+"F0.wireOp",EDGE,"E30.bottom"),sQuery(id+"F0.wireOp",EDGE,"E30.top"),sQuery(id+"F0.wireOp",EDGE,"E30.left"),sQuery(id+"F0.wireOp",EDGE,"E30.right"),sQuery(id+"F0.wireOp",EDGE,"E31.bottom"),sQuery(id+"F0.wireOp",EDGE,"E31.top"),sQuery(id+"F0.wireOp",EDGE,"E31.left"),sQuery(id+"F0.wireOp",EDGE,"E31.right"),sQuery(id+"F0.wireOp",EDGE,"E32.bottom"),sQuery(id+"F0.wireOp",EDGE,"E32.top"),sQuery(id+"F0.wireOp",EDGE,"E32.left"),sQuery(id+"F0.wireOp",EDGE,"E32.right"),sQuery(id+"F0.wireOp",EDGE,"E33.bottom"),sQuery(id+"F0.wireOp",EDGE,"E33.top"),sQuery(id+"F0.wireOp",EDGE,"E33.left"),sQuery(id+"F0.wireOp",EDGE,"E33.right"),sQuery(id+"F0.wireOp",EDGE,"E34.bottom"),sQuery(id+"F0.wireOp",EDGE,"E34.top"),sQuery(id+"F0.wireOp",EDGE,"E34.left"),sQuery(id+"F0.wireOp",EDGE,"E34.right"),sQuery(id+"F0.wireOp",EDGE,"E35.bottom"),sQuery(id+"F0.wireOp",EDGE,"E35.top"),sQuery(id+"F0.wireOp",EDGE,"E35.left"),sQuery(id+"F0.wireOp",EDGE,"E35.right"),sQuery(id+"F0.wireOp",EDGE,"E42.bottom"),sQuery(id+"F0.wireOp",EDGE,"E42.top"),sQuery(id+"F0.wireOp",EDGE,"E42.left"),sQuery(id+"F0.wireOp",EDGE,"E42.right"),sQuery(id+"F0.wireOp",EDGE,"E43.bottom"),sQuery(id+"F0.wireOp",EDGE,"E43.left"),sQuery(id+"F0.wireOp",EDGE,"E44.left"),sQuery(id+"F0.wireOp",EDGE,"E45.left"),sQuery(id+"F0.wireOp",EDGE,"E47.bottom"),sQuery(id+"F0.wireOp",EDGE,"E64"),sQuery(id+"F0.wireOp",EDGE,"E65"),sQuery(id+"F0.wireOp",EDGE,"E66"),sQuery(id+"F0.wireOp",EDGE,"E67"),sQuery(id+"F0.wireOp",EDGE,"E68"),subQ1,subQ0,sQuery(id+"F0.wireOp",EDGE,"E71"),sQuery(id+"F0.wireOp",EDGE,"E72"),sQuery(id+"F0.wireOp",EDGE,"E79"),sQuery(id+"F0.wireOp",EDGE,"E81")])],"isStart":false})],"blendedInto":[makeQuery(id+"F2.opExtrude","CAP_FACE",FACE,{"disambiguationData":[OSD([sQuery(id+"F0.wireOp",EDGE,"E0.bottom"),sQuery(id+"F0.wireOp",EDGE,"E0.left"),sQuery(id+"F0.wireOp",EDGE,"E0.right"),sQuery(id+"F0.wireOp",EDGE,"E0.top"),sQuery(id+"F0.wireOp",EDGE,"E26.bottom"),sQuery(id+"F0.wireOp",EDGE,"E26.top"),sQuery(id+"F0.wireOp",EDGE,"E26.left"),sQuery(id+"F0.wireOp",EDGE,"E26.right"),sQuery(id+"F0.wireOp",EDGE,"E29.bottom"),sQuery(id+"F0.wireOp",EDGE,"E29.top"),sQuery(id+"F0.wireOp",EDGE,"E29.left"),sQuery(id+"F0.wireOp",EDGE,"E29.right"),sQuery(id+"F0.wireOp",EDGE,"E30.bottom"),sQuery(id+"F0.wireOp",EDGE,"E30.top"),sQuery(id+"F0.wireOp",EDGE,"E30.left"),sQuery(id+"F0.wireOp",EDGE,"E30.right"),sQuery(id+"F0.wireOp",EDGE,"E31.bottom"),sQuery(id+"F0.wireOp",EDGE,"E31.top"),sQuery(id+"F0.wireOp",EDGE,"E31.left"),sQuery(id+"F0.wireOp",EDGE,"E31.right"),sQuery(id+"F0.wireOp",EDGE,"E32.bottom"),sQuery(id+"F0.wireOp",EDGE,"E32.top"),sQuery(id+"F0.wireOp",EDGE,"E32.left"),sQuery(id+"F0.wireOp",EDGE,"E32.right"),sQuery(id+"F0.wireOp",EDGE,"E33.bottom"),sQuery(id+"F0.wireOp",EDGE,"E33.top"),sQuery(id+"F0.wireOp",EDGE,"E33.left"),sQuery(id+"F0.wireOp",EDGE,"E33.right"),sQuery(id+"F0.wireOp",EDGE,"E34.bottom"),sQuery(id+"F0.wireOp",EDGE,"E34.top"),sQuery(id+"F0.wireOp",EDGE,"E34.left"),sQuery(id+"F0.wireOp",EDGE,"E34.right"),sQuery(id+"F0.wireOp",EDGE,"E35.bottom"),sQuery(id+"F0.wireOp",EDGE,"E35.top"),sQuery(id+"F0.wireOp",EDGE,"E35.left"),sQuery(id+"F0.wireOp",EDGE,"E35.right"),sQuery(id+"F0.wireOp",EDGE,"E42.bottom"),sQuery(id+"F0.wireOp",EDGE,"E42.top"),sQuery(id+"F0.wireOp",EDGE,"E42.left"),sQuery(id+"F0.wireOp",EDGE,"E42.right"),sQuery(id+"F0.wireOp",EDGE,"E43.bottom"),sQuery(id+"F0.wireOp",EDGE,"E43.left"),sQuery(id+"F0.wireOp",EDGE,"E44.left"),sQuery(id+"F0.wireOp",EDGE,"E45.left"),sQuery(id+"F0.wireOp",EDGE,"E47.bottom"),sQuery(id+"F0.wireOp",EDGE,"E64"),sQuery(id+"F0.wireOp",EDGE,"E65"),sQuery(id+"F0.wireOp",EDGE,"E66"),sQuery(id+"F0.wireOp",EDGE,"E67"),sQuery(id+"F0.wireOp",EDGE,"E68"),subQ1,subQ0,sQuery(id+"F0.wireOp",EDGE,"E71"),sQuery(id+"F0.wireOp",EDGE,"E72"),sQuery(id+"F0.wireOp",EDGE,"E79"),sQuery(id+"F0.wireOp",EDGE,"E81")])],"isStart":false})]});}
            var Q23;
            Q23=makeQuery(id+"F2.opExtrude","CAP_EDGE",EDGE,{"disambiguationData":[OSD([sQuery(id+"F0.wireOp",EDGE,"E70"),sQuery(id+"F0.wireOp",EDGE,"E71")])],"isStart":false});
            chamfer(context, id + "F8", {"entities" : qUnion([Q0, Q1, Q2, Q3, Q4, Q5, Q6, Q7, Q8, Q9, Q10, Q11, Q12, Q13, Q14, Q15, Q16, Q17, Q18, Q19, Q20, Q21, Q22, Q23]), "width" : 0.5 * mm, "tangentPropagation" : true});
        }
        {
            var Q0;
            Q0=makeQuery(id+"F3.opExtrude","CAP_EDGE",EDGE,{"disambiguationData":[OSD([sQuery(id+"F0.wireOp",EDGE,"E59.right")])],"isStart":false});
            var Q1;
            Q1=makeQuery(id+"F3.opExtrude","CAP_EDGE",EDGE,{"disambiguationData":[OSD([sQuery(id+"F0.wireOp",EDGE,"E60.bottom")])],"isStart":false});
            var Q2;
            Q2=makeQuery(id+"F3.opExtrude","CAP_EDGE",EDGE,{"disambiguationData":[OSD([sQuery(id+"F0.wireOp",EDGE,"E61.bottom")])],"isStart":false});
            var Q3;
            Q3=makeQuery(id+"F3.opExtrude","CAP_EDGE",EDGE,{"disambiguationData":[OSD([sQuery(id+"F0.wireOp",EDGE,"E63.top")])],"isStart":false});
            var Q4;
            Q4=makeQuery(id+"F3.opExtrude","CAP_EDGE",EDGE,{"disambiguationData":[OSD([sQuery(id+"F0.wireOp",EDGE,"E62.top")])],"isStart":false});
            var Q5;
            Q5=makeQuery(id+"F3.opExtrude","CAP_EDGE",EDGE,{"disambiguationData":[OSD([sQuery(id+"F0.wireOp",EDGE,"E78")])],"isStart":false});
            var Q6;
            {var subQ0=sQuery(id+"F0.wireOp",EDGE,"E78");var subQ1=sQuery(id+"F0.wireOp",EDGE,"E74");Q6=makeQuery(id+"F4.opChamfer","BLEND_EDGE",EDGE,{"blendedFrom":[makeQuery(id+"F3.opExtrude","SWEPT_EDGE",EDGE,{"disambiguationData":[OSD([subQ1,subQ0])]}),makeQuery(id+"F3.opExtrude","CAP_FACE",FACE,{"disambiguationData":[OSD([sQuery(id+"F0.wireOp",EDGE,"E43.bottom"),sQuery(id+"F0.wireOp",EDGE,"E43.left"),sQuery(id+"F0.wireOp",EDGE,"E44.left"),sQuery(id+"F0.wireOp",EDGE,"E45.left"),sQuery(id+"F0.wireOp",EDGE,"E47.bottom"),sQuery(id+"F0.wireOp",EDGE,"E59.bottom"),sQuery(id+"F0.wireOp",EDGE,"E59.top"),sQuery(id+"F0.wireOp",EDGE,"E59.left"),sQuery(id+"F0.wireOp",EDGE,"E59.right"),sQuery(id+"F0.wireOp",EDGE,"E60.bottom"),sQuery(id+"F0.wireOp",EDGE,"E60.top"),sQuery(id+"F0.wireOp",EDGE,"E60.left"),sQuery(id+"F0.wireOp",EDGE,"E60.right"),sQuery(id+"F0.wireOp",EDGE,"E61.bottom"),sQuery(id+"F0.wireOp",EDGE,"E61.top"),sQuery(id+"F0.wireOp",EDGE,"E61.left"),sQuery(id+"F0.wireOp",EDGE,"E61.right"),sQuery(id+"F0.wireOp",EDGE,"E62.bottom"),sQuery(id+"F0.wireOp",EDGE,"E62.top"),sQuery(id+"F0.wireOp",EDGE,"E62.left"),sQuery(id+"F0.wireOp",EDGE,"E62.right"),sQuery(id+"F0.wireOp",EDGE,"E63.bottom"),sQuery(id+"F0.wireOp",EDGE,"E63.top"),sQuery(id+"F0.wireOp",EDGE,"E63.left"),sQuery(id+"F0.wireOp",EDGE,"E63.right"),sQuery(id+"F0.wireOp",EDGE,"E72"),sQuery(id+"F0.wireOp",EDGE,"E73"),subQ1,sQuery(id+"F0.wireOp",EDGE,"E76"),sQuery(id+"F0.wireOp",EDGE,"E77"),subQ0,sQuery(id+"F0.wireOp",EDGE,"E79"),sQuery(id+"F0.wireOp",EDGE,"E81")])],"isStart":false})],"blendedInto":[makeQuery(id+"F3.opExtrude","CAP_FACE",FACE,{"disambiguationData":[OSD([sQuery(id+"F0.wireOp",EDGE,"E43.bottom"),sQuery(id+"F0.wireOp",EDGE,"E43.left"),sQuery(id+"F0.wireOp",EDGE,"E44.left"),sQuery(id+"F0.wireOp",EDGE,"E45.left"),sQuery(id+"F0.wireOp",EDGE,"E47.bottom"),sQuery(id+"F0.wireOp",EDGE,"E59.bottom"),sQuery(id+"F0.wireOp",EDGE,"E59.top"),sQuery(id+"F0.wireOp",EDGE,"E59.left"),sQuery(id+"F0.wireOp",EDGE,"E59.right"),sQuery(id+"F0.wireOp",EDGE,"E60.bottom"),sQuery(id+"F0.wireOp",EDGE,"E60.top"),sQuery(id+"F0.wireOp",EDGE,"E60.left"),sQuery(id+"F0.wireOp",EDGE,"E60.right"),sQuery(id+"F0.wireOp",EDGE,"E61.bottom"),sQuery(id+"F0.wireOp",EDGE,"E61.top"),sQuery(id+"F0.wireOp",EDGE,"E61.left"),sQuery(id+"F0.wireOp",EDGE,"E61.right"),sQuery(id+"F0.wireOp",EDGE,"E62.bottom"),sQuery(id+"F0.wireOp",EDGE,"E62.top"),sQuery(id+"F0.wireOp",EDGE,"E62.left"),sQuery(id+"F0.wireOp",EDGE,"E62.right"),sQuery(id+"F0.wireOp",EDGE,"E63.bottom"),sQuery(id+"F0.wireOp",EDGE,"E63.top"),sQuery(id+"F0.wireOp",EDGE,"E63.left"),sQuery(id+"F0.wireOp",EDGE,"E63.right"),sQuery(id+"F0.wireOp",EDGE,"E72"),sQuery(id+"F0.wireOp",EDGE,"E73"),subQ1,sQuery(id+"F0.wireOp",EDGE,"E76"),sQuery(id+"F0.wireOp",EDGE,"E77"),subQ0,sQuery(id+"F0.wireOp",EDGE,"E79"),sQuery(id+"F0.wireOp",EDGE,"E81")])],"isStart":false})]});}
            var Q7;
            Q7=makeQuery(id+"F3.opExtrude","CAP_EDGE",EDGE,{"disambiguationData":[OSD([sQuery(id+"F0.wireOp",EDGE,"E74")])],"isStart":false});
            var Q8;
            Q8=makeQuery(id+"F3.opExtrude","CAP_EDGE",EDGE,{"disambiguationData":[OSD([sQuery(id+"F0.wireOp",EDGE,"E72"),sQuery(id+"F0.wireOp",EDGE,"E73")])],"isStart":false});
            var Q9;
            {var subQ0=sQuery(id+"F0.wireOp",EDGE,"E74");var subQ1=sQuery(id+"F0.wireOp",EDGE,"E73");Q9=makeQuery(id+"F4.opChamfer","BLEND_EDGE",EDGE,{"blendedFrom":[makeQuery(id+"F3.opExtrude","SWEPT_EDGE",EDGE,{"disambiguationData":[OSD([subQ1,subQ0])]}),makeQuery(id+"F3.opExtrude","CAP_FACE",FACE,{"disambiguationData":[OSD([sQuery(id+"F0.wireOp",EDGE,"E43.bottom"),sQuery(id+"F0.wireOp",EDGE,"E43.left"),sQuery(id+"F0.wireOp",EDGE,"E44.left"),sQuery(id+"F0.wireOp",EDGE,"E45.left"),sQuery(id+"F0.wireOp",EDGE,"E47.bottom"),sQuery(id+"F0.wireOp",EDGE,"E59.bottom"),sQuery(id+"F0.wireOp",EDGE,"E59.top"),sQuery(id+"F0.wireOp",EDGE,"E59.left"),sQuery(id+"F0.wireOp",EDGE,"E59.right"),sQuery(id+"F0.wireOp",EDGE,"E60.bottom"),sQuery(id+"F0.wireOp",EDGE,"E60.top"),sQuery(id+"F0.wireOp",EDGE,"E60.left"),sQuery(id+"F0.wireOp",EDGE,"E60.right"),sQuery(id+"F0.wireOp",EDGE,"E61.bottom"),sQuery(id+"F0.wireOp",EDGE,"E61.top"),sQuery(id+"F0.wireOp",EDGE,"E61.left"),sQuery(id+"F0.wireOp",EDGE,"E61.right"),sQuery(id+"F0.wireOp",EDGE,"E62.bottom"),sQuery(id+"F0.wireOp",EDGE,"E62.top"),sQuery(id+"F0.wireOp",EDGE,"E62.left"),sQuery(id+"F0.wireOp",EDGE,"E62.right"),sQuery(id+"F0.wireOp",EDGE,"E63.bottom"),sQuery(id+"F0.wireOp",EDGE,"E63.top"),sQuery(id+"F0.wireOp",EDGE,"E63.left"),sQuery(id+"F0.wireOp",EDGE,"E63.right"),sQuery(id+"F0.wireOp",EDGE,"E72"),subQ1,subQ0,sQuery(id+"F0.wireOp",EDGE,"E76"),sQuery(id+"F0.wireOp",EDGE,"E77"),sQuery(id+"F0.wireOp",EDGE,"E78"),sQuery(id+"F0.wireOp",EDGE,"E79"),sQuery(id+"F0.wireOp",EDGE,"E81")])],"isStart":false})],"blendedInto":[makeQuery(id+"F3.opExtrude","CAP_FACE",FACE,{"disambiguationData":[OSD([sQuery(id+"F0.wireOp",EDGE,"E43.bottom"),sQuery(id+"F0.wireOp",EDGE,"E43.left"),sQuery(id+"F0.wireOp",EDGE,"E44.left"),sQuery(id+"F0.wireOp",EDGE,"E45.left"),sQuery(id+"F0.wireOp",EDGE,"E47.bottom"),sQuery(id+"F0.wireOp",EDGE,"E59.bottom"),sQuery(id+"F0.wireOp",EDGE,"E59.top"),sQuery(id+"F0.wireOp",EDGE,"E59.left"),sQuery(id+"F0.wireOp",EDGE,"E59.right"),sQuery(id+"F0.wireOp",EDGE,"E60.bottom"),sQuery(id+"F0.wireOp",EDGE,"E60.top"),sQuery(id+"F0.wireOp",EDGE,"E60.left"),sQuery(id+"F0.wireOp",EDGE,"E60.right"),sQuery(id+"F0.wireOp",EDGE,"E61.bottom"),sQuery(id+"F0.wireOp",EDGE,"E61.top"),sQuery(id+"F0.wireOp",EDGE,"E61.left"),sQuery(id+"F0.wireOp",EDGE,"E61.right"),sQuery(id+"F0.wireOp",EDGE,"E62.bottom"),sQuery(id+"F0.wireOp",EDGE,"E62.top"),sQuery(id+"F0.wireOp",EDGE,"E62.left"),sQuery(id+"F0.wireOp",EDGE,"E62.right"),sQuery(id+"F0.wireOp",EDGE,"E63.bottom"),sQuery(id+"F0.wireOp",EDGE,"E63.top"),sQuery(id+"F0.wireOp",EDGE,"E63.left"),sQuery(id+"F0.wireOp",EDGE,"E63.right"),sQuery(id+"F0.wireOp",EDGE,"E72"),subQ1,subQ0,sQuery(id+"F0.wireOp",EDGE,"E76"),sQuery(id+"F0.wireOp",EDGE,"E77"),sQuery(id+"F0.wireOp",EDGE,"E78"),sQuery(id+"F0.wireOp",EDGE,"E79"),sQuery(id+"F0.wireOp",EDGE,"E81")])],"isStart":false})]});}
            var Q10;
            Q10=makeQuery(id+"F3.opExtrude","CAP_EDGE",EDGE,{"disambiguationData":[OSD([sQuery(id+"F0.wireOp",EDGE,"E76"),sQuery(id+"F0.wireOp",EDGE,"E77")])],"isStart":false});
            var Q11;
            {var subQ0=sQuery(id+"F0.wireOp",EDGE,"E78");var subQ1=sQuery(id+"F0.wireOp",EDGE,"E77");Q11=makeQuery(id+"F4.opChamfer","BLEND_EDGE",EDGE,{"blendedFrom":[makeQuery(id+"F3.opExtrude","SWEPT_EDGE",EDGE,{"disambiguationData":[OSD([subQ1,subQ0])]}),makeQuery(id+"F3.opExtrude","CAP_FACE",FACE,{"disambiguationData":[OSD([sQuery(id+"F0.wireOp",EDGE,"E43.bottom"),sQuery(id+"F0.wireOp",EDGE,"E43.left"),sQuery(id+"F0.wireOp",EDGE,"E44.left"),sQuery(id+"F0.wireOp",EDGE,"E45.left"),sQuery(id+"F0.wireOp",EDGE,"E47.bottom"),sQuery(id+"F0.wireOp",EDGE,"E59.bottom"),sQuery(id+"F0.wireOp",EDGE,"E59.top"),sQuery(id+"F0.wireOp",EDGE,"E59.left"),sQuery(id+"F0.wireOp",EDGE,"E59.right"),sQuery(id+"F0.wireOp",EDGE,"E60.bottom"),sQuery(id+"F0.wireOp",EDGE,"E60.top"),sQuery(id+"F0.wireOp",EDGE,"E60.left"),sQuery(id+"F0.wireOp",EDGE,"E60.right"),sQuery(id+"F0.wireOp",EDGE,"E61.bottom"),sQuery(id+"F0.wireOp",EDGE,"E61.top"),sQuery(id+"F0.wireOp",EDGE,"E61.left"),sQuery(id+"F0.wireOp",EDGE,"E61.right"),sQuery(id+"F0.wireOp",EDGE,"E62.bottom"),sQuery(id+"F0.wireOp",EDGE,"E62.top"),sQuery(id+"F0.wireOp",EDGE,"E62.left"),sQuery(id+"F0.wireOp",EDGE,"E62.right"),sQuery(id+"F0.wireOp",EDGE,"E63.bottom"),sQuery(id+"F0.wireOp",EDGE,"E63.top"),sQuery(id+"F0.wireOp",EDGE,"E63.left"),sQuery(id+"F0.wireOp",EDGE,"E63.right"),sQuery(id+"F0.wireOp",EDGE,"E72"),sQuery(id+"F0.wireOp",EDGE,"E73"),sQuery(id+"F0.wireOp",EDGE,"E74"),sQuery(id+"F0.wireOp",EDGE,"E76"),subQ1,subQ0,sQuery(id+"F0.wireOp",EDGE,"E79"),sQuery(id+"F0.wireOp",EDGE,"E81")])],"isStart":false})],"blendedInto":[makeQuery(id+"F3.opExtrude","CAP_FACE",FACE,{"disambiguationData":[OSD([sQuery(id+"F0.wireOp",EDGE,"E43.bottom"),sQuery(id+"F0.wireOp",EDGE,"E43.left"),sQuery(id+"F0.wireOp",EDGE,"E44.left"),sQuery(id+"F0.wireOp",EDGE,"E45.left"),sQuery(id+"F0.wireOp",EDGE,"E47.bottom"),sQuery(id+"F0.wireOp",EDGE,"E59.bottom"),sQuery(id+"F0.wireOp",EDGE,"E59.top"),sQuery(id+"F0.wireOp",EDGE,"E59.left"),sQuery(id+"F0.wireOp",EDGE,"E59.right"),sQuery(id+"F0.wireOp",EDGE,"E60.bottom"),sQuery(id+"F0.wireOp",EDGE,"E60.top"),sQuery(id+"F0.wireOp",EDGE,"E60.left"),sQuery(id+"F0.wireOp",EDGE,"E60.right"),sQuery(id+"F0.wireOp",EDGE,"E61.bottom"),sQuery(id+"F0.wireOp",EDGE,"E61.top"),sQuery(id+"F0.wireOp",EDGE,"E61.left"),sQuery(id+"F0.wireOp",EDGE,"E61.right"),sQuery(id+"F0.wireOp",EDGE,"E62.bottom"),sQuery(id+"F0.wireOp",EDGE,"E62.top"),sQuery(id+"F0.wireOp",EDGE,"E62.left"),sQuery(id+"F0.wireOp",EDGE,"E62.right"),sQuery(id+"F0.wireOp",EDGE,"E63.bottom"),sQuery(id+"F0.wireOp",EDGE,"E63.top"),sQuery(id+"F0.wireOp",EDGE,"E63.left"),sQuery(id+"F0.wireOp",EDGE,"E63.right"),sQuery(id+"F0.wireOp",EDGE,"E72"),sQuery(id+"F0.wireOp",EDGE,"E73"),sQuery(id+"F0.wireOp",EDGE,"E74"),sQuery(id+"F0.wireOp",EDGE,"E76"),subQ1,subQ0,sQuery(id+"F0.wireOp",EDGE,"E79"),sQuery(id+"F0.wireOp",EDGE,"E81")])],"isStart":false})]});}
            chamfer(context, id + "F9", {"entities" : qUnion([Q0, Q1, Q2, Q3, Q4, Q5, Q6, Q7, Q8, Q9, Q10, Q11]), "width" : 0.3 * mm, "tangentPropagation" : true});
        }
    });
